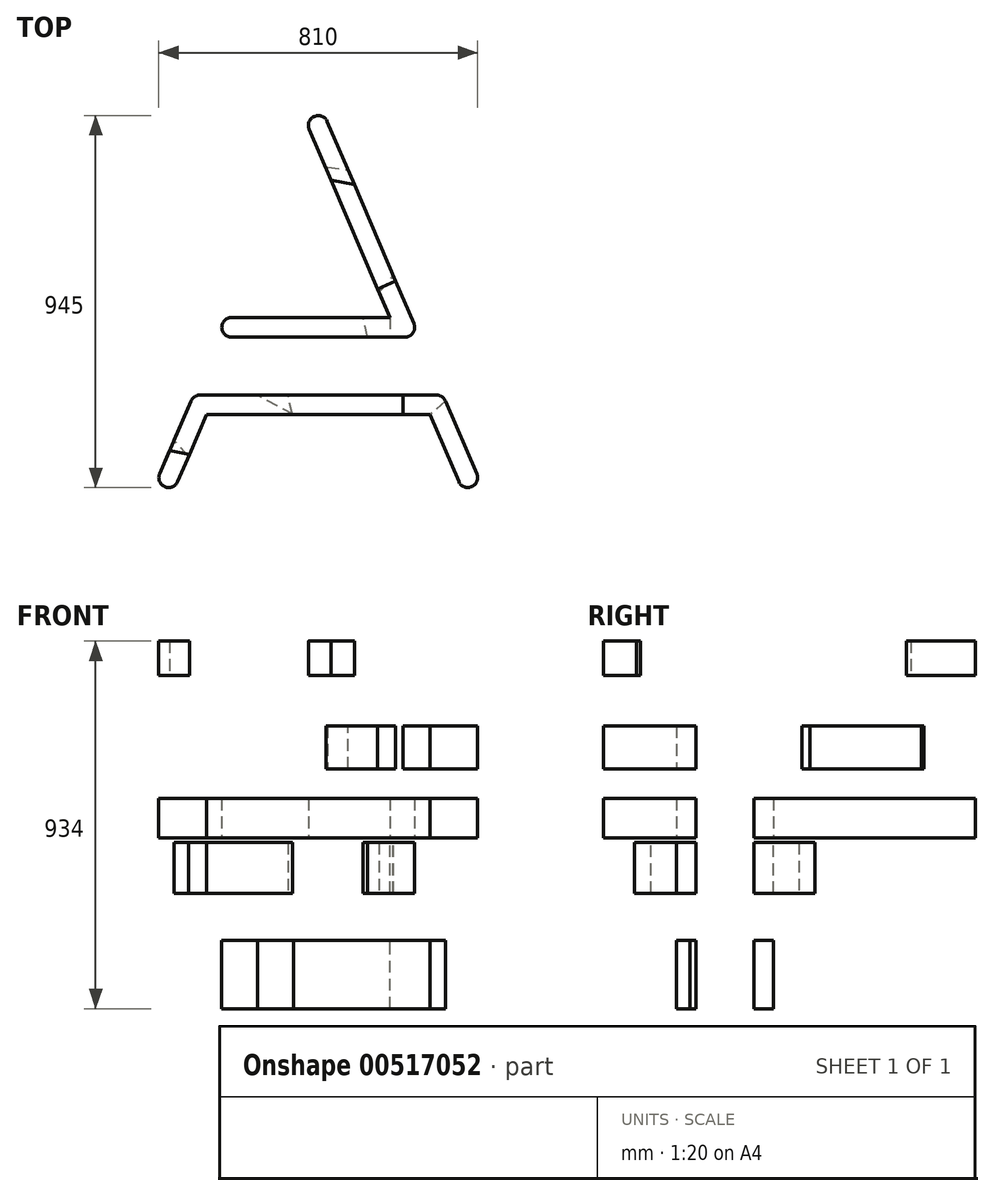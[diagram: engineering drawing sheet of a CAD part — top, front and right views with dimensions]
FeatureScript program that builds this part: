
annotation { "Feature Type Name" : "Feature", "Feature Type Description" : "" }
export const myFeature = defineFeature(function(context is Context, id is Id, definition is map)
    precondition{}
    {
        {
            var Q0;
            Q0=qCreatedBy(makeId("Top.planeOp"),FACE);
            var sketch = newSketch(context, id + "F0", { "sketchPlane" : qUnion([Q0])});
            skLineSegment(sketch, "E0", {"start": v(4.38, -239.2) * mm, "end": v(22.85, -239.2) * mm});
            skLineSegment(sketch, "E1", {"start": v(22.85, -239.2) * mm, "end": v(41.32, -239.2) * mm});
            skLineSegment(sketch, "E2", {"start": v(41.32, -239.2) * mm, "end": v(59.79, -239.2) * mm});
            skLineSegment(sketch, "E3", {"start": v(59.79, -239.2) * mm, "end": v(78.26, -239.2) * mm});
            skLineSegment(sketch, "E4", {"start": v(78.26, -239.2) * mm, "end": v(96.73, -239.2) * mm});
            skLineSegment(sketch, "E5", {"start": v(96.73, -239.2) * mm, "end": v(115.2, -239.2) * mm});
            skLineSegment(sketch, "E6", {"start": v(115.2, -239.2) * mm, "end": v(133.66, -239.2) * mm});
            skLineSegment(sketch, "E7", {"start": v(133.66, -239.2) * mm, "end": v(152.13, -239.2) * mm});
            skLineSegment(sketch, "E8", {"start": v(152.13, -239.2) * mm, "end": v(170.6, -239.2) * mm});
            skLineSegment(sketch, "E9", {"start": v(170.6, -239.2) * mm, "end": v(189.07, -239.2) * mm});
            skLineSegment(sketch, "E10", {"start": v(189.07, -239.2) * mm, "end": v(207.53, -239.2) * mm});
            skLineSegment(sketch, "E11", {"start": v(207.53, -239.2) * mm, "end": v(226, -239.2) * mm});
            skLineSegment(sketch, "E12", {"start": v(226, -239.2) * mm, "end": v(244.47, -239.2) * mm});
            skLineSegment(sketch, "E13", {"start": v(244.47, -239.2) * mm, "end": v(262.94, -239.2) * mm});
            skLineSegment(sketch, "E14", {"start": v(262.94, -239.2) * mm, "end": v(281.4, -239.2) * mm});
            skLineSegment(sketch, "E15", {"start": v(281.4, -239.2) * mm, "end": v(299.88, -239.2) * mm});
            skLineSegment(sketch, "E16", {"start": v(299.88, -239.2) * mm, "end": v(302.32, -239.25) * mm});
            skLineSegment(sketch, "E17", {"start": v(302.32, -239.25) * mm, "end": v(304.6, -239.4) * mm});
            skLineSegment(sketch, "E18", {"start": v(304.6, -239.4) * mm, "end": v(306.73, -239.65) * mm});
            skLineSegment(sketch, "E19", {"start": v(306.73, -239.65) * mm, "end": v(308.7, -240.02) * mm});
            skLineSegment(sketch, "E20", {"start": v(308.7, -240.02) * mm, "end": v(310.55, -240.51) * mm});
            skLineSegment(sketch, "E21", {"start": v(310.55, -240.51) * mm, "end": v(312.26, -241.13) * mm});
            skLineSegment(sketch, "E22", {"start": v(312.26, -241.13) * mm, "end": v(313.86, -241.89) * mm});
            skLineSegment(sketch, "E23", {"start": v(313.86, -241.89) * mm, "end": v(315.35, -242.78) * mm});
            skLineSegment(sketch, "E24", {"start": v(315.35, -242.78) * mm, "end": v(316.74, -243.83) * mm});
            skLineSegment(sketch, "E25", {"start": v(316.74, -243.83) * mm, "end": v(318.05, -245.03) * mm});
            skLineSegment(sketch, "E26", {"start": v(318.05, -245.03) * mm, "end": v(319.27, -246.39) * mm});
            skLineSegment(sketch, "E27", {"start": v(319.27, -246.39) * mm, "end": v(320.43, -247.92) * mm});
            skLineSegment(sketch, "E28", {"start": v(320.43, -247.92) * mm, "end": v(321.53, -249.63) * mm});
            skLineSegment(sketch, "E29", {"start": v(321.53, -249.63) * mm, "end": v(322.58, -251.52) * mm});
            skLineSegment(sketch, "E30", {"start": v(322.58, -251.52) * mm, "end": v(323.6, -253.6) * mm});
            skLineSegment(sketch, "E31", {"start": v(323.6, -253.6) * mm, "end": v(324.58, -255.88) * mm});
            skLineSegment(sketch, "E32", {"start": v(324.58, -255.88) * mm, "end": v(329.18, -267.18) * mm});
            skLineSegment(sketch, "E33", {"start": v(329.18, -267.18) * mm, "end": v(333.78, -278.48) * mm});
            skLineSegment(sketch, "E34", {"start": v(333.78, -278.48) * mm, "end": v(338.38, -289.78) * mm});
            skLineSegment(sketch, "E35", {"start": v(338.38, -289.78) * mm, "end": v(342.98, -301.08) * mm});
            skLineSegment(sketch, "E36", {"start": v(342.98, -301.08) * mm, "end": v(347.58, -312.38) * mm});
            skLineSegment(sketch, "E37", {"start": v(347.58, -312.38) * mm, "end": v(352.18, -323.68) * mm});
            skLineSegment(sketch, "E38", {"start": v(352.18, -323.68) * mm, "end": v(356.78, -334.98) * mm});
            skLineSegment(sketch, "E39", {"start": v(356.78, -334.98) * mm, "end": v(361.37, -346.29) * mm});
            skLineSegment(sketch, "E40", {"start": v(361.37, -346.29) * mm, "end": v(365.97, -357.59) * mm});
            skLineSegment(sketch, "E41", {"start": v(365.97, -357.59) * mm, "end": v(370.57, -368.89) * mm});
            skLineSegment(sketch, "E42", {"start": v(370.57, -368.89) * mm, "end": v(375.16, -380.19) * mm});
            skLineSegment(sketch, "E43", {"start": v(375.16, -380.19) * mm, "end": v(379.76, -391.5) * mm});
            skLineSegment(sketch, "E44", {"start": v(379.76, -391.5) * mm, "end": v(384.35, -402.8) * mm});
            skLineSegment(sketch, "E45", {"start": v(384.35, -402.8) * mm, "end": v(388.95, -414.1) * mm});
            skLineSegment(sketch, "E46", {"start": v(388.95, -414.1) * mm, "end": v(393.54, -425.4) * mm});
            skLineSegment(sketch, "E47", {"start": v(393.54, -425.4) * mm, "end": v(398.13, -436.7) * mm});
            skLineSegment(sketch, "E48", {"start": v(398.13, -436.7) * mm, "end": v(399, -439.11) * mm});
            skLineSegment(sketch, "E49", {"start": v(399, -439.11) * mm, "end": v(399.66, -441.5) * mm});
            skLineSegment(sketch, "E50", {"start": v(399.66, -441.5) * mm, "end": v(400.09, -443.83) * mm});
            skLineSegment(sketch, "E51", {"start": v(400.09, -443.83) * mm, "end": v(400.3, -446.11) * mm});
            skLineSegment(sketch, "E52", {"start": v(400.3, -446.11) * mm, "end": v(400.3, -448.34) * mm});
            skLineSegment(sketch, "E53", {"start": v(400.3, -448.34) * mm, "end": v(400.08, -450.5) * mm});
            skLineSegment(sketch, "E54", {"start": v(400.08, -450.5) * mm, "end": v(399.65, -452.58) * mm});
            skLineSegment(sketch, "E55", {"start": v(399.65, -452.58) * mm, "end": v(399.02, -454.58) * mm});
            skLineSegment(sketch, "E56", {"start": v(399.02, -454.58) * mm, "end": v(398.19, -456.5) * mm});
            skLineSegment(sketch, "E57", {"start": v(398.19, -456.5) * mm, "end": v(397.16, -458.3) * mm});
            skLineSegment(sketch, "E58", {"start": v(397.16, -458.3) * mm, "end": v(395.93, -460.01) * mm});
            skLineSegment(sketch, "E59", {"start": v(395.93, -460.01) * mm, "end": v(394.51, -461.6) * mm});
            skLineSegment(sketch, "E60", {"start": v(394.51, -461.6) * mm, "end": v(392.9, -463.08) * mm});
            skLineSegment(sketch, "E61", {"start": v(392.9, -463.08) * mm, "end": v(391.1, -464.41) * mm});
            skLineSegment(sketch, "E62", {"start": v(391.1, -464.41) * mm, "end": v(389.13, -465.61) * mm});
            skLineSegment(sketch, "E63", {"start": v(389.13, -465.61) * mm, "end": v(386.97, -466.67) * mm});
            skLineSegment(sketch, "E64", {"start": v(386.97, -466.67) * mm, "end": v(384.89, -467.45) * mm});
            skLineSegment(sketch, "E65", {"start": v(384.89, -467.45) * mm, "end": v(382.79, -468.02) * mm});
            skLineSegment(sketch, "E66", {"start": v(382.79, -468.02) * mm, "end": v(380.69, -468.35) * mm});
            skLineSegment(sketch, "E67", {"start": v(380.69, -468.35) * mm, "end": v(378.6, -468.47) * mm});
            skLineSegment(sketch, "E68", {"start": v(378.6, -468.47) * mm, "end": v(376.53, -468.36) * mm});
            skLineSegment(sketch, "E69", {"start": v(376.53, -468.36) * mm, "end": v(374.5, -468.05) * mm});
            skLineSegment(sketch, "E70", {"start": v(374.5, -468.05) * mm, "end": v(372.5, -467.52) * mm});
            skLineSegment(sketch, "E71", {"start": v(372.5, -467.52) * mm, "end": v(370.56, -466.79) * mm});
            skLineSegment(sketch, "E72", {"start": v(370.56, -466.79) * mm, "end": v(368.69, -465.85) * mm});
            skLineSegment(sketch, "E73", {"start": v(368.69, -465.85) * mm, "end": v(366.9, -464.71) * mm});
            skLineSegment(sketch, "E74", {"start": v(366.9, -464.71) * mm, "end": v(365.19, -463.38) * mm});
            skLineSegment(sketch, "E75", {"start": v(365.19, -463.38) * mm, "end": v(363.58, -461.85) * mm});
            skLineSegment(sketch, "E76", {"start": v(363.58, -461.85) * mm, "end": v(362.08, -460.13) * mm});
            skLineSegment(sketch, "E77", {"start": v(362.08, -460.13) * mm, "end": v(360.71, -458.23) * mm});
            skLineSegment(sketch, "E78", {"start": v(360.71, -458.23) * mm, "end": v(359.47, -456.14) * mm});
            skLineSegment(sketch, "E79", {"start": v(359.47, -456.14) * mm, "end": v(358.38, -453.87) * mm});
            skLineSegment(sketch, "E80", {"start": v(358.38, -453.87) * mm, "end": v(356.95, -450.55) * mm});
            skLineSegment(sketch, "E81", {"start": v(356.95, -450.55) * mm, "end": v(355.54, -447.22) * mm});
            skLineSegment(sketch, "E82", {"start": v(355.54, -447.22) * mm, "end": v(354.13, -443.88) * mm});
            skLineSegment(sketch, "E83", {"start": v(354.13, -443.88) * mm, "end": v(352.74, -440.54) * mm});
            skLineSegment(sketch, "E84", {"start": v(352.74, -440.54) * mm, "end": v(351.36, -437.2) * mm});
            skLineSegment(sketch, "E85", {"start": v(351.36, -437.2) * mm, "end": v(349.98, -433.85) * mm});
            skLineSegment(sketch, "E86", {"start": v(349.98, -433.85) * mm, "end": v(348.61, -430.5) * mm});
            skLineSegment(sketch, "E87", {"start": v(348.61, -430.5) * mm, "end": v(347.25, -427.14) * mm});
            skLineSegment(sketch, "E88", {"start": v(347.25, -427.14) * mm, "end": v(345.9, -423.79) * mm});
            skLineSegment(sketch, "E89", {"start": v(345.9, -423.79) * mm, "end": v(344.54, -420.43) * mm});
            skLineSegment(sketch, "E90", {"start": v(344.54, -420.43) * mm, "end": v(343.19, -417.07) * mm});
            skLineSegment(sketch, "E91", {"start": v(343.19, -417.07) * mm, "end": v(341.83, -413.71) * mm});
            skLineSegment(sketch, "E92", {"start": v(341.83, -413.71) * mm, "end": v(340.48, -410.36) * mm});
            skLineSegment(sketch, "E93", {"start": v(340.48, -410.36) * mm, "end": v(339.13, -407) * mm});
            skLineSegment(sketch, "E94", {"start": v(339.13, -407) * mm, "end": v(337.77, -403.64) * mm});
            skLineSegment(sketch, "E95", {"start": v(337.77, -403.64) * mm, "end": v(336.4, -400.29) * mm});
            skLineSegment(sketch, "E96", {"start": v(336.4, -400.29) * mm, "end": v(333.53, -393.2) * mm});
            skLineSegment(sketch, "E97", {"start": v(333.53, -393.2) * mm, "end": v(330.65, -386.13) * mm});
            skLineSegment(sketch, "E98", {"start": v(330.65, -386.13) * mm, "end": v(327.76, -379.05) * mm});
            skLineSegment(sketch, "E99", {"start": v(327.76, -379.05) * mm, "end": v(324.88, -371.96) * mm});
            skLineSegment(sketch, "E100", {"start": v(324.88, -371.96) * mm, "end": v(322, -364.88) * mm});
            skLineSegment(sketch, "E101", {"start": v(322, -364.88) * mm, "end": v(319.12, -357.8) * mm});
            skLineSegment(sketch, "E102", {"start": v(319.12, -357.8) * mm, "end": v(316.24, -350.72) * mm});
            skLineSegment(sketch, "E103", {"start": v(316.24, -350.72) * mm, "end": v(313.37, -343.63) * mm});
            skLineSegment(sketch, "E104", {"start": v(313.37, -343.63) * mm, "end": v(310.5, -336.55) * mm});
            skLineSegment(sketch, "E105", {"start": v(310.5, -336.55) * mm, "end": v(307.62, -329.47) * mm});
            skLineSegment(sketch, "E106", {"start": v(307.62, -329.47) * mm, "end": v(304.74, -322.38) * mm});
            skLineSegment(sketch, "E107", {"start": v(304.74, -322.38) * mm, "end": v(301.87, -315.3) * mm});
            skLineSegment(sketch, "E108", {"start": v(301.87, -315.3) * mm, "end": v(299, -308.2) * mm});
            skLineSegment(sketch, "E109", {"start": v(299, -308.2) * mm, "end": v(296.14, -301.12) * mm});
            skLineSegment(sketch, "E110", {"start": v(296.14, -301.12) * mm, "end": v(293.28, -294.03) * mm});
            skLineSegment(sketch, "E111", {"start": v(293.28, -294.03) * mm, "end": v(290.42, -286.94) * mm});
            skLineSegment(sketch, "E112", {"start": v(290.42, -286.94) * mm, "end": v(290.17, -286.36) * mm});
            skLineSegment(sketch, "E113", {"start": v(290.17, -286.36) * mm, "end": v(289.91, -285.82) * mm});
            skLineSegment(sketch, "E114", {"start": v(289.91, -285.82) * mm, "end": v(289.64, -285.32) * mm});
            skLineSegment(sketch, "E115", {"start": v(289.64, -285.32) * mm, "end": v(289.36, -284.87) * mm});
            skLineSegment(sketch, "E116", {"start": v(289.36, -284.87) * mm, "end": v(289.07, -284.46) * mm});
            skLineSegment(sketch, "E117", {"start": v(289.07, -284.46) * mm, "end": v(288.75, -284.1) * mm});
            skLineSegment(sketch, "E118", {"start": v(288.75, -284.1) * mm, "end": v(288.41, -283.77) * mm});
            skLineSegment(sketch, "E119", {"start": v(288.41, -283.77) * mm, "end": v(288.05, -283.48) * mm});
            skLineSegment(sketch, "E120", {"start": v(288.05, -283.48) * mm, "end": v(287.66, -283.23) * mm});
            skLineSegment(sketch, "E121", {"start": v(287.66, -283.23) * mm, "end": v(287.24, -283.02) * mm});
            skLineSegment(sketch, "E122", {"start": v(287.24, -283.02) * mm, "end": v(286.78, -282.84) * mm});
            skLineSegment(sketch, "E123", {"start": v(286.78, -282.84) * mm, "end": v(286.3, -282.7) * mm});
            skLineSegment(sketch, "E124", {"start": v(286.3, -282.7) * mm, "end": v(285.77, -282.6) * mm});
            skLineSegment(sketch, "E125", {"start": v(285.77, -282.6) * mm, "end": v(285.2, -282.51) * mm});
            skLineSegment(sketch, "E126", {"start": v(285.2, -282.51) * mm, "end": v(284.59, -282.47) * mm});
            skLineSegment(sketch, "E127", {"start": v(284.59, -282.47) * mm, "end": v(283.93, -282.46) * mm});
            skLineSegment(sketch, "E128", {"start": v(283.93, -282.46) * mm, "end": v(261.52, -282.47) * mm});
            skLineSegment(sketch, "E129", {"start": v(261.52, -282.47) * mm, "end": v(239.12, -282.48) * mm});
            skLineSegment(sketch, "E130", {"start": v(239.12, -282.48) * mm, "end": v(216.71, -282.48) * mm});
            skLineSegment(sketch, "E131", {"start": v(216.71, -282.48) * mm, "end": v(194.3, -282.49) * mm});
            skLineSegment(sketch, "E132", {"start": v(194.3, -282.49) * mm, "end": v(171.9, -282.49) * mm});
            skLineSegment(sketch, "E133", {"start": v(171.9, -282.49) * mm, "end": v(149.5, -282.49) * mm});
            skLineSegment(sketch, "E134", {"start": v(149.5, -282.49) * mm, "end": v(127.1, -282.49) * mm});
            skLineSegment(sketch, "E135", {"start": v(127.1, -282.49) * mm, "end": v(104.69, -282.48) * mm});
            skLineSegment(sketch, "E136", {"start": v(104.69, -282.48) * mm, "end": v(82.28, -282.48) * mm});
            skLineSegment(sketch, "E137", {"start": v(82.28, -282.48) * mm, "end": v(59.88, -282.47) * mm});
            skLineSegment(sketch, "E138", {"start": v(59.88, -282.47) * mm, "end": v(37.47, -282.47) * mm});
            skLineSegment(sketch, "E139", {"start": v(37.47, -282.47) * mm, "end": v(15.07, -282.46) * mm});
            skLineSegment(sketch, "E140", {"start": v(15.07, -282.46) * mm, "end": v(-7.34, -282.46) * mm});
            skLineSegment(sketch, "E141", {"start": v(-7.34, -282.46) * mm, "end": v(-29.74, -282.45) * mm});
            skLineSegment(sketch, "E142", {"start": v(-29.74, -282.45) * mm, "end": v(-52.15, -282.45) * mm});
            skLineSegment(sketch, "E143", {"start": v(-52.15, -282.45) * mm, "end": v(-74.56, -282.45) * mm});
            skLineSegment(sketch, "E144", {"start": v(-74.56, -282.45) * mm, "end": v(-87.15, -282.45) * mm});
            skLineSegment(sketch, "E145", {"start": v(-87.15, -282.45) * mm, "end": v(-99.74, -282.45) * mm});
            skLineSegment(sketch, "E146", {"start": v(-99.74, -282.45) * mm, "end": v(-112.33, -282.45) * mm});
            skLineSegment(sketch, "E147", {"start": v(-112.33, -282.45) * mm, "end": v(-124.93, -282.46) * mm});
            skLineSegment(sketch, "E148", {"start": v(-124.93, -282.46) * mm, "end": v(-137.52, -282.47) * mm});
            skLineSegment(sketch, "E149", {"start": v(-137.52, -282.47) * mm, "end": v(-150.11, -282.47) * mm});
            skLineSegment(sketch, "E150", {"start": v(-150.11, -282.47) * mm, "end": v(-162.7, -282.48) * mm});
            skLineSegment(sketch, "E151", {"start": v(-162.7, -282.48) * mm, "end": v(-175.3, -282.48) * mm});
            skLineSegment(sketch, "E152", {"start": v(-175.3, -282.48) * mm, "end": v(-187.9, -282.49) * mm});
            skLineSegment(sketch, "E153", {"start": v(-187.9, -282.49) * mm, "end": v(-200.49, -282.49) * mm});
            skLineSegment(sketch, "E154", {"start": v(-200.49, -282.49) * mm, "end": v(-213.08, -282.5) * mm});
            skLineSegment(sketch, "E155", {"start": v(-213.08, -282.5) * mm, "end": v(-225.67, -282.49) * mm});
            skLineSegment(sketch, "E156", {"start": v(-225.67, -282.49) * mm, "end": v(-238.26, -282.48) * mm});
            skLineSegment(sketch, "E157", {"start": v(-238.26, -282.48) * mm, "end": v(-250.86, -282.47) * mm});
            skLineSegment(sketch, "E158", {"start": v(-250.86, -282.47) * mm, "end": v(-263.45, -282.46) * mm});
            skLineSegment(sketch, "E159", {"start": v(-263.45, -282.46) * mm, "end": v(-276.04, -282.44) * mm});
            skLineSegment(sketch, "E160", {"start": v(-276.04, -282.44) * mm, "end": v(-276.75, -282.46) * mm});
            skLineSegment(sketch, "E161", {"start": v(-276.75, -282.46) * mm, "end": v(-277.42, -282.5) * mm});
            skLineSegment(sketch, "E162", {"start": v(-277.42, -282.5) * mm, "end": v(-278.05, -282.57) * mm});
            skLineSegment(sketch, "E163", {"start": v(-278.05, -282.57) * mm, "end": v(-278.63, -282.68) * mm});
            skLineSegment(sketch, "E164", {"start": v(-278.63, -282.68) * mm, "end": v(-279.18, -282.81) * mm});
            skLineSegment(sketch, "E165", {"start": v(-279.18, -282.81) * mm, "end": v(-279.7, -283) * mm});
            skLineSegment(sketch, "E166", {"start": v(-279.7, -283) * mm, "end": v(-280.17, -283.2) * mm});
            skLineSegment(sketch, "E167", {"start": v(-280.17, -283.2) * mm, "end": v(-280.62, -283.46) * mm});
            skLineSegment(sketch, "E168", {"start": v(-280.62, -283.46) * mm, "end": v(-281.05, -283.75) * mm});
            skLineSegment(sketch, "E169", {"start": v(-281.05, -283.75) * mm, "end": v(-281.45, -284.1) * mm});
            skLineSegment(sketch, "E170", {"start": v(-281.45, -284.1) * mm, "end": v(-281.83, -284.48) * mm});
            skLineSegment(sketch, "E171", {"start": v(-281.83, -284.48) * mm, "end": v(-282.18, -284.91) * mm});
            skLineSegment(sketch, "E172", {"start": v(-282.18, -284.91) * mm, "end": v(-282.53, -285.4) * mm});
            skLineSegment(sketch, "E173", {"start": v(-282.53, -285.4) * mm, "end": v(-282.85, -285.93) * mm});
            skLineSegment(sketch, "E174", {"start": v(-282.85, -285.93) * mm, "end": v(-283.17, -286.52) * mm});
            skLineSegment(sketch, "E175", {"start": v(-283.17, -286.52) * mm, "end": v(-283.48, -287.16) * mm});
            skLineSegment(sketch, "E176", {"start": v(-283.48, -287.16) * mm, "end": v(-288.23, -297.71) * mm});
            skLineSegment(sketch, "E177", {"start": v(-288.23, -297.71) * mm, "end": v(-293, -308.27) * mm});
            skLineSegment(sketch, "E178", {"start": v(-293, -308.27) * mm, "end": v(-297.76, -318.82) * mm});
            skLineSegment(sketch, "E179", {"start": v(-297.76, -318.82) * mm, "end": v(-302.52, -329.37) * mm});
            skLineSegment(sketch, "E180", {"start": v(-302.52, -329.37) * mm, "end": v(-307.3, -339.92) * mm});
            skLineSegment(sketch, "E181", {"start": v(-307.3, -339.92) * mm, "end": v(-312.06, -350.46) * mm});
            skLineSegment(sketch, "E182", {"start": v(-312.06, -350.46) * mm, "end": v(-316.84, -361.01) * mm});
            skLineSegment(sketch, "E183", {"start": v(-316.84, -361.01) * mm, "end": v(-321.61, -371.56) * mm});
            skLineSegment(sketch, "E184", {"start": v(-321.61, -371.56) * mm, "end": v(-326.39, -382.1) * mm});
            skLineSegment(sketch, "E185", {"start": v(-326.39, -382.1) * mm, "end": v(-331.17, -392.65) * mm});
            skLineSegment(sketch, "E186", {"start": v(-331.17, -392.65) * mm, "end": v(-335.95, -403.2) * mm});
            skLineSegment(sketch, "E187", {"start": v(-335.95, -403.2) * mm, "end": v(-340.73, -413.74) * mm});
            skLineSegment(sketch, "E188", {"start": v(-340.73, -413.74) * mm, "end": v(-345.5, -424.28) * mm});
            skLineSegment(sketch, "E189", {"start": v(-345.5, -424.28) * mm, "end": v(-350.29, -434.82) * mm});
            skLineSegment(sketch, "E190", {"start": v(-350.29, -434.82) * mm, "end": v(-355.07, -445.37) * mm});
            skLineSegment(sketch, "E191", {"start": v(-355.07, -445.37) * mm, "end": v(-359.85, -455.9) * mm});
            skLineSegment(sketch, "E192", {"start": v(-359.85, -455.9) * mm, "end": v(-360.64, -457.5) * mm});
            skLineSegment(sketch, "E193", {"start": v(-360.64, -457.5) * mm, "end": v(-361.53, -458.99) * mm});
            skLineSegment(sketch, "E194", {"start": v(-361.53, -458.99) * mm, "end": v(-362.51, -460.37) * mm});
            skLineSegment(sketch, "E195", {"start": v(-362.51, -460.37) * mm, "end": v(-363.58, -461.65) * mm});
            skLineSegment(sketch, "E196", {"start": v(-363.58, -461.65) * mm, "end": v(-364.73, -462.83) * mm});
            skLineSegment(sketch, "E197", {"start": v(-364.73, -462.83) * mm, "end": v(-365.96, -463.9) * mm});
            skLineSegment(sketch, "E198", {"start": v(-365.96, -463.9) * mm, "end": v(-367.26, -464.85) * mm});
            skLineSegment(sketch, "E199", {"start": v(-367.26, -464.85) * mm, "end": v(-368.64, -465.7) * mm});
            skLineSegment(sketch, "E200", {"start": v(-368.64, -465.7) * mm, "end": v(-370.09, -466.42) * mm});
            skLineSegment(sketch, "E201", {"start": v(-370.09, -466.42) * mm, "end": v(-371.6, -467.03) * mm});
            skLineSegment(sketch, "E202", {"start": v(-371.6, -467.03) * mm, "end": v(-373.17, -467.53) * mm});
            skLineSegment(sketch, "E203", {"start": v(-373.17, -467.53) * mm, "end": v(-374.8, -467.9) * mm});
            skLineSegment(sketch, "E204", {"start": v(-374.8, -467.9) * mm, "end": v(-376.47, -468.15) * mm});
            skLineSegment(sketch, "E205", {"start": v(-376.47, -468.15) * mm, "end": v(-378.2, -468.28) * mm});
            skLineSegment(sketch, "E206", {"start": v(-378.2, -468.28) * mm, "end": v(-379.96, -468.29) * mm});
            skLineSegment(sketch, "E207", {"start": v(-379.96, -468.29) * mm, "end": v(-381.77, -468.16) * mm});
            skLineSegment(sketch, "E208", {"start": v(-381.77, -468.16) * mm, "end": v(-383.48, -467.92) * mm});
            skLineSegment(sketch, "E209", {"start": v(-383.48, -467.92) * mm, "end": v(-385.15, -467.57) * mm});
            skLineSegment(sketch, "E210", {"start": v(-385.15, -467.57) * mm, "end": v(-386.78, -467.1) * mm});
            skLineSegment(sketch, "E211", {"start": v(-386.78, -467.1) * mm, "end": v(-388.34, -466.53) * mm});
            skLineSegment(sketch, "E212", {"start": v(-388.34, -466.53) * mm, "end": v(-389.84, -465.85) * mm});
            skLineSegment(sketch, "E213", {"start": v(-389.84, -465.85) * mm, "end": v(-391.27, -465.07) * mm});
            skLineSegment(sketch, "E214", {"start": v(-391.27, -465.07) * mm, "end": v(-392.63, -464.19) * mm});
            skLineSegment(sketch, "E215", {"start": v(-392.63, -464.19) * mm, "end": v(-393.89, -463.21) * mm});
            skLineSegment(sketch, "E216", {"start": v(-393.89, -463.21) * mm, "end": v(-395.06, -462.14) * mm});
            skLineSegment(sketch, "E217", {"start": v(-395.06, -462.14) * mm, "end": v(-396.13, -460.98) * mm});
            skLineSegment(sketch, "E218", {"start": v(-396.13, -460.98) * mm, "end": v(-397.08, -459.74) * mm});
            skLineSegment(sketch, "E219", {"start": v(-397.08, -459.74) * mm, "end": v(-397.92, -458.4) * mm});
            skLineSegment(sketch, "E220", {"start": v(-397.92, -458.4) * mm, "end": v(-398.64, -457) * mm});
            skLineSegment(sketch, "E221", {"start": v(-398.64, -457) * mm, "end": v(-399.22, -455.51) * mm});
            skLineSegment(sketch, "E222", {"start": v(-399.22, -455.51) * mm, "end": v(-399.66, -453.95) * mm});
            skLineSegment(sketch, "E223", {"start": v(-399.66, -453.95) * mm, "end": v(-399.96, -452.32) * mm});
            skLineSegment(sketch, "E224", {"start": v(-399.96, -452.32) * mm, "end": v(-400.08, -451.27) * mm});
            skLineSegment(sketch, "E225", {"start": v(-400.08, -451.27) * mm, "end": v(-400.18, -450.2) * mm});
            skLineSegment(sketch, "E226", {"start": v(-400.18, -450.2) * mm, "end": v(-400.25, -449.13) * mm});
            skLineSegment(sketch, "E227", {"start": v(-400.25, -449.13) * mm, "end": v(-400.29, -448.04) * mm});
            skLineSegment(sketch, "E228", {"start": v(-400.29, -448.04) * mm, "end": v(-400.3, -446.94) * mm});
            skLineSegment(sketch, "E229", {"start": v(-400.3, -446.94) * mm, "end": v(-400.28, -445.84) * mm});
            skLineSegment(sketch, "E230", {"start": v(-400.28, -445.84) * mm, "end": v(-400.22, -444.73) * mm});
            skLineSegment(sketch, "E231", {"start": v(-400.22, -444.73) * mm, "end": v(-400.14, -443.63) * mm});
            skLineSegment(sketch, "E232", {"start": v(-400.14, -443.63) * mm, "end": v(-400.02, -442.53) * mm});
            skLineSegment(sketch, "E233", {"start": v(-400.02, -442.53) * mm, "end": v(-399.86, -441.45) * mm});
            skLineSegment(sketch, "E234", {"start": v(-399.86, -441.45) * mm, "end": v(-399.67, -440.38) * mm});
            skLineSegment(sketch, "E235", {"start": v(-399.67, -440.38) * mm, "end": v(-399.43, -439.32) * mm});
            skLineSegment(sketch, "E236", {"start": v(-399.43, -439.32) * mm, "end": v(-399.16, -438.29) * mm});
            skLineSegment(sketch, "E237", {"start": v(-399.16, -438.29) * mm, "end": v(-398.85, -437.28) * mm});
            skLineSegment(sketch, "E238", {"start": v(-398.85, -437.28) * mm, "end": v(-398.5, -436.3) * mm});
            skLineSegment(sketch, "E239", {"start": v(-398.5, -436.3) * mm, "end": v(-398.1, -435.34) * mm});
            skLineSegment(sketch, "E240", {"start": v(-398.1, -435.34) * mm, "end": v(-392.92, -423.78) * mm});
            skLineSegment(sketch, "E241", {"start": v(-392.92, -423.78) * mm, "end": v(-387.74, -412.22) * mm});
            skLineSegment(sketch, "E242", {"start": v(-387.74, -412.22) * mm, "end": v(-382.54, -400.66) * mm});
            skLineSegment(sketch, "E243", {"start": v(-382.54, -400.66) * mm, "end": v(-377.34, -389.1) * mm});
            skLineSegment(sketch, "E244", {"start": v(-377.34, -389.1) * mm, "end": v(-372.13, -377.56) * mm});
            skLineSegment(sketch, "E245", {"start": v(-372.13, -377.56) * mm, "end": v(-366.91, -366.01) * mm});
            skLineSegment(sketch, "E246", {"start": v(-366.91, -366.01) * mm, "end": v(-361.69, -354.47) * mm});
            skLineSegment(sketch, "E247", {"start": v(-361.69, -354.47) * mm, "end": v(-356.46, -342.93) * mm});
            skLineSegment(sketch, "E248", {"start": v(-356.46, -342.93) * mm, "end": v(-351.23, -331.39) * mm});
            skLineSegment(sketch, "E249", {"start": v(-351.23, -331.39) * mm, "end": v(-346, -319.85) * mm});
            skLineSegment(sketch, "E250", {"start": v(-346, -319.85) * mm, "end": v(-340.76, -308.31) * mm});
            skLineSegment(sketch, "E251", {"start": v(-340.76, -308.31) * mm, "end": v(-335.52, -296.77) * mm});
            skLineSegment(sketch, "E252", {"start": v(-335.52, -296.77) * mm, "end": v(-330.28, -285.24) * mm});
            skLineSegment(sketch, "E253", {"start": v(-330.28, -285.24) * mm, "end": v(-325.04, -273.7) * mm});
            skLineSegment(sketch, "E254", {"start": v(-325.04, -273.7) * mm, "end": v(-319.8, -262.17) * mm});
            skLineSegment(sketch, "E255", {"start": v(-319.8, -262.17) * mm, "end": v(-314.56, -250.63) * mm});
            skLineSegment(sketch, "E256", {"start": v(-314.56, -250.63) * mm, "end": v(-313.9, -249.32) * mm});
            skLineSegment(sketch, "E257", {"start": v(-313.9, -249.32) * mm, "end": v(-313.2, -248.1) * mm});
            skLineSegment(sketch, "E258", {"start": v(-313.2, -248.1) * mm, "end": v(-312.43, -246.97) * mm});
            skLineSegment(sketch, "E259", {"start": v(-312.43, -246.97) * mm, "end": v(-311.6, -245.91) * mm});
            skLineSegment(sketch, "E260", {"start": v(-311.6, -245.91) * mm, "end": v(-310.72, -244.94) * mm});
            skLineSegment(sketch, "E261", {"start": v(-310.72, -244.94) * mm, "end": v(-309.78, -244.05) * mm});
            skLineSegment(sketch, "E262", {"start": v(-309.78, -244.05) * mm, "end": v(-308.79, -243.24) * mm});
            skLineSegment(sketch, "E263", {"start": v(-308.79, -243.24) * mm, "end": v(-307.74, -242.51) * mm});
            skLineSegment(sketch, "E264", {"start": v(-307.74, -242.51) * mm, "end": v(-306.64, -241.86) * mm});
            skLineSegment(sketch, "E265", {"start": v(-306.64, -241.86) * mm, "end": v(-305.49, -241.28) * mm});
            skLineSegment(sketch, "E266", {"start": v(-305.49, -241.28) * mm, "end": v(-304.29, -240.77) * mm});
            skLineSegment(sketch, "E267", {"start": v(-304.29, -240.77) * mm, "end": v(-303.04, -240.34) * mm});
            skLineSegment(sketch, "E268", {"start": v(-303.04, -240.34) * mm, "end": v(-301.74, -239.97) * mm});
            skLineSegment(sketch, "E269", {"start": v(-301.74, -239.97) * mm, "end": v(-300.4, -239.68) * mm});
            skLineSegment(sketch, "E270", {"start": v(-300.4, -239.68) * mm, "end": v(-299.03, -239.45) * mm});
            skLineSegment(sketch, "E271", {"start": v(-299.03, -239.45) * mm, "end": v(-297.6, -239.3) * mm});
            skLineSegment(sketch, "E272", {"start": v(-297.6, -239.3) * mm, "end": v(-297.2, -239.26) * mm});
            skLineSegment(sketch, "E273", {"start": v(-297.2, -239.26) * mm, "end": v(-296.8, -239.24) * mm});
            skLineSegment(sketch, "E274", {"start": v(-296.8, -239.24) * mm, "end": v(-296.4, -239.21) * mm});
            skLineSegment(sketch, "E275", {"start": v(-296.4, -239.21) * mm, "end": v(-295.99, -239.2) * mm});
            skLineSegment(sketch, "E276", {"start": v(-295.99, -239.2) * mm, "end": v(-295.58, -239.19) * mm});
            skLineSegment(sketch, "E277", {"start": v(-295.58, -239.19) * mm, "end": v(-295.17, -239.18) * mm});
            skLineSegment(sketch, "E278", {"start": v(-295.17, -239.18) * mm, "end": v(-294.77, -239.18) * mm});
            skLineSegment(sketch, "E279", {"start": v(-294.77, -239.18) * mm, "end": v(-294.36, -239.18) * mm});
            skLineSegment(sketch, "E280", {"start": v(-294.36, -239.18) * mm, "end": v(-293.95, -239.18) * mm});
            skLineSegment(sketch, "E281", {"start": v(-293.95, -239.18) * mm, "end": v(-293.55, -239.18) * mm});
            skLineSegment(sketch, "E282", {"start": v(-293.55, -239.18) * mm, "end": v(-293.14, -239.19) * mm});
            skLineSegment(sketch, "E283", {"start": v(-293.14, -239.19) * mm, "end": v(-292.73, -239.2) * mm});
            skLineSegment(sketch, "E284", {"start": v(-292.73, -239.2) * mm, "end": v(-292.33, -239.2) * mm});
            skLineSegment(sketch, "E285", {"start": v(-292.33, -239.2) * mm, "end": v(-291.92, -239.2) * mm});
            skLineSegment(sketch, "E286", {"start": v(-291.92, -239.2) * mm, "end": v(-291.51, -239.2) * mm});
            skLineSegment(sketch, "E287", {"start": v(-291.51, -239.2) * mm, "end": v(-291.1, -239.2) * mm});
            skLineSegment(sketch, "E288", {"start": v(-291.1, -239.2) * mm, "end": v(-272.64, -239.2) * mm});
            skLineSegment(sketch, "E289", {"start": v(-272.64, -239.2) * mm, "end": v(-254.17, -239.2) * mm});
            skLineSegment(sketch, "E290", {"start": v(-254.17, -239.2) * mm, "end": v(-235.7, -239.2) * mm});
            skLineSegment(sketch, "E291", {"start": v(-235.7, -239.2) * mm, "end": v(-217.23, -239.2) * mm});
            skLineSegment(sketch, "E292", {"start": v(-217.23, -239.2) * mm, "end": v(-198.77, -239.2) * mm});
            skLineSegment(sketch, "E293", {"start": v(-198.77, -239.2) * mm, "end": v(-180.3, -239.2) * mm});
            skLineSegment(sketch, "E294", {"start": v(-180.3, -239.2) * mm, "end": v(-161.83, -239.2) * mm});
            skLineSegment(sketch, "E295", {"start": v(-161.83, -239.2) * mm, "end": v(-143.36, -239.2) * mm});
            skLineSegment(sketch, "E296", {"start": v(-143.36, -239.2) * mm, "end": v(-124.9, -239.2) * mm});
            skLineSegment(sketch, "E297", {"start": v(-124.9, -239.2) * mm, "end": v(-106.43, -239.2) * mm});
            skLineSegment(sketch, "E298", {"start": v(-106.43, -239.2) * mm, "end": v(-87.96, -239.2) * mm});
            skLineSegment(sketch, "E299", {"start": v(-87.96, -239.2) * mm, "end": v(-69.49, -239.2) * mm});
            skLineSegment(sketch, "E300", {"start": v(-69.49, -239.2) * mm, "end": v(-51.02, -239.2) * mm});
            skLineSegment(sketch, "E301", {"start": v(-51.02, -239.2) * mm, "end": v(-32.55, -239.2) * mm});
            skLineSegment(sketch, "E302", {"start": v(-32.55, -239.2) * mm, "end": v(-14.08, -239.2) * mm});
            skLineSegment(sketch, "E303", {"start": v(-14.08, -239.2) * mm, "end": v(4.38, -239.2) * mm});
            skLineSegment(sketch, "E304", {"start": v(190.22, -42.46) * mm, "end": v(190.07, -42.05) * mm});
            skLineSegment(sketch, "E305", {"start": v(190.07, -42.05) * mm, "end": v(189.92, -41.65) * mm});
            skLineSegment(sketch, "E306", {"start": v(189.92, -41.65) * mm, "end": v(189.78, -41.26) * mm});
            skLineSegment(sketch, "E307", {"start": v(189.78, -41.26) * mm, "end": v(189.64, -40.88) * mm});
            skLineSegment(sketch, "E308", {"start": v(189.64, -40.88) * mm, "end": v(189.5, -40.51) * mm});
            skLineSegment(sketch, "E309", {"start": v(189.5, -40.51) * mm, "end": v(189.38, -40.15) * mm});
            skLineSegment(sketch, "E310", {"start": v(189.38, -40.15) * mm, "end": v(189.25, -39.8) * mm});
            skLineSegment(sketch, "E311", {"start": v(189.25, -39.8) * mm, "end": v(189.12, -39.46) * mm});
            skLineSegment(sketch, "E312", {"start": v(189.12, -39.46) * mm, "end": v(189, -39.12) * mm});
            skLineSegment(sketch, "E313", {"start": v(189, -39.12) * mm, "end": v(188.87, -38.79) * mm});
            skLineSegment(sketch, "E314", {"start": v(188.87, -38.79) * mm, "end": v(188.75, -38.46) * mm});
            skLineSegment(sketch, "E315", {"start": v(188.75, -38.46) * mm, "end": v(188.63, -38.14) * mm});
            skLineSegment(sketch, "E316", {"start": v(188.63, -38.14) * mm, "end": v(188.5, -37.82) * mm});
            skLineSegment(sketch, "E317", {"start": v(188.5, -37.82) * mm, "end": v(188.39, -37.5) * mm});
            skLineSegment(sketch, "E318", {"start": v(188.39, -37.5) * mm, "end": v(188.26, -37.2) * mm});
            skLineSegment(sketch, "E319", {"start": v(188.26, -37.2) * mm, "end": v(188.14, -36.88) * mm});
            skLineSegment(sketch, "E320", {"start": v(188.14, -36.88) * mm, "end": v(179.93, -16.85) * mm});
            skLineSegment(sketch, "E321", {"start": v(179.93, -16.85) * mm, "end": v(171.72, 3.2) * mm});
            skLineSegment(sketch, "E322", {"start": v(171.72, 3.2) * mm, "end": v(163.5, 23.23) * mm});
            skLineSegment(sketch, "E323", {"start": v(163.5, 23.23) * mm, "end": v(155.3, 43.27) * mm});
            skLineSegment(sketch, "E324", {"start": v(155.3, 43.27) * mm, "end": v(147.09, 63.3) * mm});
            skLineSegment(sketch, "E325", {"start": v(147.09, 63.3) * mm, "end": v(138.88, 83.34) * mm});
            skLineSegment(sketch, "E326", {"start": v(138.88, 83.34) * mm, "end": v(130.67, 103.38) * mm});
            skLineSegment(sketch, "E327", {"start": v(130.67, 103.38) * mm, "end": v(122.46, 123.42) * mm});
            skLineSegment(sketch, "E328", {"start": v(122.46, 123.42) * mm, "end": v(114.25, 143.45) * mm});
            skLineSegment(sketch, "E329", {"start": v(114.25, 143.45) * mm, "end": v(106.04, 163.5) * mm});
            skLineSegment(sketch, "E330", {"start": v(106.04, 163.5) * mm, "end": v(97.83, 183.53) * mm});
            skLineSegment(sketch, "E331", {"start": v(97.83, 183.53) * mm, "end": v(89.62, 203.57) * mm});
            skLineSegment(sketch, "E332", {"start": v(89.62, 203.57) * mm, "end": v(81.4, 223.6) * mm});
            skLineSegment(sketch, "E333", {"start": v(81.4, 223.6) * mm, "end": v(73.2, 243.64) * mm});
            skLineSegment(sketch, "E334", {"start": v(73.2, 243.64) * mm, "end": v(64.99, 263.68) * mm});
            skLineSegment(sketch, "E335", {"start": v(64.99, 263.68) * mm, "end": v(56.78, 283.72) * mm});
            skLineSegment(sketch, "E336", {"start": v(56.78, 283.72) * mm, "end": v(52.9, 293.19) * mm});
            skLineSegment(sketch, "E337", {"start": v(52.9, 293.19) * mm, "end": v(49.02, 302.66) * mm});
            skLineSegment(sketch, "E338", {"start": v(49.02, 302.66) * mm, "end": v(45.15, 312.13) * mm});
            skLineSegment(sketch, "E339", {"start": v(45.15, 312.13) * mm, "end": v(41.28, 321.6) * mm});
            skLineSegment(sketch, "E340", {"start": v(41.28, 321.6) * mm, "end": v(37.41, 331.07) * mm});
            skLineSegment(sketch, "E341", {"start": v(37.41, 331.07) * mm, "end": v(33.54, 340.55) * mm});
            skLineSegment(sketch, "E342", {"start": v(33.54, 340.55) * mm, "end": v(29.67, 350.02) * mm});
            skLineSegment(sketch, "E343", {"start": v(29.67, 350.02) * mm, "end": v(25.8, 359.5) * mm});
            skLineSegment(sketch, "E344", {"start": v(25.8, 359.5) * mm, "end": v(21.92, 368.96) * mm});
            skLineSegment(sketch, "E345", {"start": v(21.92, 368.96) * mm, "end": v(18.04, 378.43) * mm});
            skLineSegment(sketch, "E346", {"start": v(18.04, 378.43) * mm, "end": v(14.15, 387.9) * mm});
            skLineSegment(sketch, "E347", {"start": v(14.15, 387.9) * mm, "end": v(10.26, 397.36) * mm});
            skLineSegment(sketch, "E348", {"start": v(10.26, 397.36) * mm, "end": v(6.35, 406.81) * mm});
            skLineSegment(sketch, "E349", {"start": v(6.35, 406.81) * mm, "end": v(2.44, 416.27) * mm});
            skLineSegment(sketch, "E350", {"start": v(2.44, 416.27) * mm, "end": v(-1.48, 425.72) * mm});
            skLineSegment(sketch, "E351", {"start": v(-1.48, 425.72) * mm, "end": v(-5.41, 435.17) * mm});
            skLineSegment(sketch, "E352", {"start": v(-5.41, 435.17) * mm, "end": v(-6.4, 437.74) * mm});
            skLineSegment(sketch, "E353", {"start": v(-6.4, 437.74) * mm, "end": v(-7.16, 440.17) * mm});
            skLineSegment(sketch, "E354", {"start": v(-7.16, 440.17) * mm, "end": v(-7.7, 442.45) * mm});
            skLineSegment(sketch, "E355", {"start": v(-7.7, 442.45) * mm, "end": v(-8.06, 444.6) * mm});
            skLineSegment(sketch, "E356", {"start": v(-8.06, 444.6) * mm, "end": v(-8.22, 446.62) * mm});
            skLineSegment(sketch, "E357", {"start": v(-8.22, 446.62) * mm, "end": v(-8.2, 448.52) * mm});
            skLineSegment(sketch, "E358", {"start": v(-8.2, 448.52) * mm, "end": v(-8.02, 450.3) * mm});
            skLineSegment(sketch, "E359", {"start": v(-8.02, 450.3) * mm, "end": v(-7.68, 451.98) * mm});
            skLineSegment(sketch, "E360", {"start": v(-7.68, 451.98) * mm, "end": v(-7.21, 453.56) * mm});
            skLineSegment(sketch, "E361", {"start": v(-7.21, 453.56) * mm, "end": v(-6.62, 455.05) * mm});
            skLineSegment(sketch, "E362", {"start": v(-6.62, 455.05) * mm, "end": v(-5.9, 456.46) * mm});
            skLineSegment(sketch, "E363", {"start": v(-5.9, 456.46) * mm, "end": v(-5.1, 457.78) * mm});
            skLineSegment(sketch, "E364", {"start": v(-5.1, 457.78) * mm, "end": v(-4.2, 459.03) * mm});
            skLineSegment(sketch, "E365", {"start": v(-4.2, 459.03) * mm, "end": v(-3.22, 460.22) * mm});
            skLineSegment(sketch, "E366", {"start": v(-3.22, 460.22) * mm, "end": v(-2.18, 461.36) * mm});
            skLineSegment(sketch, "E367", {"start": v(-2.18, 461.36) * mm, "end": v(-1.1, 462.44) * mm});
            skLineSegment(sketch, "E368", {"start": v(-1.1, 462.44) * mm, "end": v(0.6, 463.9) * mm});
            skLineSegment(sketch, "E369", {"start": v(0.6, 463.9) * mm, "end": v(2.37, 465.17) * mm});
            skLineSegment(sketch, "E370", {"start": v(2.37, 465.17) * mm, "end": v(4.22, 466.23) * mm});
            skLineSegment(sketch, "E371", {"start": v(4.22, 466.23) * mm, "end": v(6.13, 467.09) * mm});
            skLineSegment(sketch, "E372", {"start": v(6.13, 467.09) * mm, "end": v(8.09, 467.74) * mm});
            skLineSegment(sketch, "E373", {"start": v(8.09, 467.74) * mm, "end": v(10.08, 468.18) * mm});
            skLineSegment(sketch, "E374", {"start": v(10.08, 468.18) * mm, "end": v(12.08, 468.43) * mm});
            skLineSegment(sketch, "E375", {"start": v(12.08, 468.43) * mm, "end": v(14.1, 468.47) * mm});
            skLineSegment(sketch, "E376", {"start": v(14.1, 468.47) * mm, "end": v(16.1, 468.3) * mm});
            skLineSegment(sketch, "E377", {"start": v(16.1, 468.3) * mm, "end": v(18.08, 467.93) * mm});
            skLineSegment(sketch, "E378", {"start": v(18.08, 467.93) * mm, "end": v(20.02, 467.36) * mm});
            skLineSegment(sketch, "E379", {"start": v(20.02, 467.36) * mm, "end": v(21.92, 466.58) * mm});
            skLineSegment(sketch, "E380", {"start": v(21.92, 466.58) * mm, "end": v(23.76, 465.6) * mm});
            skLineSegment(sketch, "E381", {"start": v(23.76, 465.6) * mm, "end": v(25.51, 464.41) * mm});
            skLineSegment(sketch, "E382", {"start": v(25.51, 464.41) * mm, "end": v(27.18, 463.02) * mm});
            skLineSegment(sketch, "E383", {"start": v(27.18, 463.02) * mm, "end": v(28.75, 461.43) * mm});
            skLineSegment(sketch, "E384", {"start": v(28.75, 461.43) * mm, "end": v(29.28, 460.8) * mm});
            skLineSegment(sketch, "E385", {"start": v(29.28, 460.8) * mm, "end": v(29.8, 460.16) * mm});
            skLineSegment(sketch, "E386", {"start": v(29.8, 460.16) * mm, "end": v(30.31, 459.5) * mm});
            skLineSegment(sketch, "E387", {"start": v(30.31, 459.5) * mm, "end": v(30.8, 458.83) * mm});
            skLineSegment(sketch, "E388", {"start": v(30.8, 458.83) * mm, "end": v(31.28, 458.14) * mm});
            skLineSegment(sketch, "E389", {"start": v(31.28, 458.14) * mm, "end": v(31.74, 457.43) * mm});
            skLineSegment(sketch, "E390", {"start": v(31.74, 457.43) * mm, "end": v(32.18, 456.72) * mm});
            skLineSegment(sketch, "E391", {"start": v(32.18, 456.72) * mm, "end": v(32.61, 456) * mm});
            skLineSegment(sketch, "E392", {"start": v(32.61, 456) * mm, "end": v(33.03, 455.25) * mm});
            skLineSegment(sketch, "E393", {"start": v(33.03, 455.25) * mm, "end": v(33.43, 454.5) * mm});
            skLineSegment(sketch, "E394", {"start": v(33.43, 454.5) * mm, "end": v(33.82, 453.76) * mm});
            skLineSegment(sketch, "E395", {"start": v(33.82, 453.76) * mm, "end": v(34.2, 453) * mm});
            skLineSegment(sketch, "E396", {"start": v(34.2, 453) * mm, "end": v(34.56, 452.24) * mm});
            skLineSegment(sketch, "E397", {"start": v(34.56, 452.24) * mm, "end": v(34.9, 451.48) * mm});
            skLineSegment(sketch, "E398", {"start": v(34.9, 451.48) * mm, "end": v(35.24, 450.7) * mm});
            skLineSegment(sketch, "E399", {"start": v(35.24, 450.7) * mm, "end": v(35.56, 449.94) * mm});
            skLineSegment(sketch, "E400", {"start": v(35.56, 449.94) * mm, "end": v(44.72, 427.63) * mm});
            skLineSegment(sketch, "E401", {"start": v(44.72, 427.63) * mm, "end": v(53.87, 405.32) * mm});
            skLineSegment(sketch, "E402", {"start": v(53.87, 405.32) * mm, "end": v(63.03, 383) * mm});
            skLineSegment(sketch, "E403", {"start": v(63.03, 383) * mm, "end": v(72.18, 360.69) * mm});
            skLineSegment(sketch, "E404", {"start": v(72.18, 360.69) * mm, "end": v(81.33, 338.37) * mm});
            skLineSegment(sketch, "E405", {"start": v(81.33, 338.37) * mm, "end": v(90.48, 316.06) * mm});
            skLineSegment(sketch, "E406", {"start": v(90.48, 316.06) * mm, "end": v(99.63, 293.74) * mm});
            skLineSegment(sketch, "E407", {"start": v(99.63, 293.74) * mm, "end": v(108.78, 271.43) * mm});
            skLineSegment(sketch, "E408", {"start": v(108.78, 271.43) * mm, "end": v(117.92, 249.1) * mm});
            skLineSegment(sketch, "E409", {"start": v(117.92, 249.1) * mm, "end": v(127.07, 226.79) * mm});
            skLineSegment(sketch, "E410", {"start": v(127.07, 226.79) * mm, "end": v(136.21, 204.47) * mm});
            skLineSegment(sketch, "E411", {"start": v(136.21, 204.47) * mm, "end": v(145.36, 182.15) * mm});
            skLineSegment(sketch, "E412", {"start": v(145.36, 182.15) * mm, "end": v(154.5, 159.83) * mm});
            skLineSegment(sketch, "E413", {"start": v(154.5, 159.83) * mm, "end": v(163.64, 137.52) * mm});
            skLineSegment(sketch, "E414", {"start": v(163.64, 137.52) * mm, "end": v(172.79, 115.2) * mm});
            skLineSegment(sketch, "E415", {"start": v(172.79, 115.2) * mm, "end": v(181.93, 92.88) * mm});
            skLineSegment(sketch, "E416", {"start": v(181.93, 92.88) * mm, "end": v(185.72, 83.61) * mm});
            skLineSegment(sketch, "E417", {"start": v(185.72, 83.61) * mm, "end": v(189.5, 74.34) * mm});
            skLineSegment(sketch, "E418", {"start": v(189.5, 74.34) * mm, "end": v(193.29, 65.07) * mm});
            skLineSegment(sketch, "E419", {"start": v(193.29, 65.07) * mm, "end": v(197.06, 55.8) * mm});
            skLineSegment(sketch, "E420", {"start": v(197.06, 55.8) * mm, "end": v(200.84, 46.52) * mm});
            skLineSegment(sketch, "E421", {"start": v(200.84, 46.52) * mm, "end": v(204.62, 37.24) * mm});
            skLineSegment(sketch, "E422", {"start": v(204.62, 37.24) * mm, "end": v(208.4, 27.97) * mm});
            skLineSegment(sketch, "E423", {"start": v(208.4, 27.97) * mm, "end": v(212.18, 18.7) * mm});
            skLineSegment(sketch, "E424", {"start": v(212.18, 18.7) * mm, "end": v(215.97, 9.43) * mm});
            skLineSegment(sketch, "E425", {"start": v(215.97, 9.43) * mm, "end": v(219.77, 0.17) * mm});
            skLineSegment(sketch, "E426", {"start": v(219.77, 0.17) * mm, "end": v(223.58, -9.1) * mm});
            skLineSegment(sketch, "E427", {"start": v(223.58, -9.1) * mm, "end": v(227.4, -18.35) * mm});
            skLineSegment(sketch, "E428", {"start": v(227.4, -18.35) * mm, "end": v(231.23, -27.6) * mm});
            skLineSegment(sketch, "E429", {"start": v(231.23, -27.6) * mm, "end": v(235.08, -36.85) * mm});
            skLineSegment(sketch, "E430", {"start": v(235.08, -36.85) * mm, "end": v(238.94, -46.09) * mm});
            skLineSegment(sketch, "E431", {"start": v(238.94, -46.09) * mm, "end": v(242.82, -55.32) * mm});
            skLineSegment(sketch, "E432", {"start": v(242.82, -55.32) * mm, "end": v(243.94, -58.51) * mm});
            skLineSegment(sketch, "E433", {"start": v(243.94, -58.51) * mm, "end": v(244.57, -61.61) * mm});
            skLineSegment(sketch, "E434", {"start": v(244.57, -61.61) * mm, "end": v(244.75, -64.6) * mm});
            skLineSegment(sketch, "E435", {"start": v(244.75, -64.6) * mm, "end": v(244.52, -67.46) * mm});
            skLineSegment(sketch, "E436", {"start": v(244.52, -67.46) * mm, "end": v(243.91, -70.18) * mm});
            skLineSegment(sketch, "E437", {"start": v(243.91, -70.18) * mm, "end": v(242.96, -72.74) * mm});
            skLineSegment(sketch, "E438", {"start": v(242.96, -72.74) * mm, "end": v(241.71, -75.12) * mm});
            skLineSegment(sketch, "E439", {"start": v(241.71, -75.12) * mm, "end": v(240.19, -77.32) * mm});
            skLineSegment(sketch, "E440", {"start": v(240.19, -77.32) * mm, "end": v(238.43, -79.3) * mm});
            skLineSegment(sketch, "E441", {"start": v(238.43, -79.3) * mm, "end": v(236.47, -81.07) * mm});
            skLineSegment(sketch, "E442", {"start": v(236.47, -81.07) * mm, "end": v(234.36, -82.6) * mm});
            skLineSegment(sketch, "E443", {"start": v(234.36, -82.6) * mm, "end": v(232.1, -83.88) * mm});
            skLineSegment(sketch, "E444", {"start": v(232.1, -83.88) * mm, "end": v(229.77, -84.89) * mm});
            skLineSegment(sketch, "E445", {"start": v(229.77, -84.89) * mm, "end": v(227.37, -85.61) * mm});
            skLineSegment(sketch, "E446", {"start": v(227.37, -85.61) * mm, "end": v(224.96, -86.04) * mm});
            skLineSegment(sketch, "E447", {"start": v(224.96, -86.04) * mm, "end": v(222.56, -86.15) * mm});
            skLineSegment(sketch, "E448", {"start": v(222.56, -86.15) * mm, "end": v(222.4, -86.14) * mm});
            skLineSegment(sketch, "E449", {"start": v(222.4, -86.14) * mm, "end": v(222.24, -86.14) * mm});
            skLineSegment(sketch, "E450", {"start": v(222.24, -86.14) * mm, "end": v(222.09, -86.14) * mm});
            skLineSegment(sketch, "E451", {"start": v(222.09, -86.14) * mm, "end": v(221.93, -86.14) * mm});
            skLineSegment(sketch, "E452", {"start": v(221.93, -86.14) * mm, "end": v(221.77, -86.14) * mm});
            skLineSegment(sketch, "E453", {"start": v(221.77, -86.14) * mm, "end": v(221.62, -86.14) * mm});
            skLineSegment(sketch, "E454", {"start": v(221.62, -86.14) * mm, "end": v(221.46, -86.14) * mm});
            skLineSegment(sketch, "E455", {"start": v(221.46, -86.14) * mm, "end": v(221.3, -86.14) * mm});
            skLineSegment(sketch, "E456", {"start": v(221.3, -86.14) * mm, "end": v(221.15, -86.14) * mm});
            skLineSegment(sketch, "E457", {"start": v(221.15, -86.14) * mm, "end": v(221, -86.14) * mm});
            skLineSegment(sketch, "E458", {"start": v(221, -86.14) * mm, "end": v(220.84, -86.14) * mm});
            skLineSegment(sketch, "E459", {"start": v(220.84, -86.14) * mm, "end": v(220.68, -86.15) * mm});
            skLineSegment(sketch, "E460", {"start": v(220.68, -86.15) * mm, "end": v(220.52, -86.15) * mm});
            skLineSegment(sketch, "E461", {"start": v(220.52, -86.15) * mm, "end": v(220.37, -86.15) * mm});
            skLineSegment(sketch, "E462", {"start": v(220.37, -86.15) * mm, "end": v(220.21, -86.15) * mm});
            skLineSegment(sketch, "E463", {"start": v(220.21, -86.15) * mm, "end": v(220.06, -86.15) * mm});
            skLineSegment(sketch, "E464", {"start": v(220.06, -86.15) * mm, "end": v(193.53, -86.15) * mm});
            skLineSegment(sketch, "E465", {"start": v(193.53, -86.15) * mm, "end": v(167, -86.15) * mm});
            skLineSegment(sketch, "E466", {"start": v(167, -86.15) * mm, "end": v(140.47, -86.15) * mm});
            skLineSegment(sketch, "E467", {"start": v(140.47, -86.15) * mm, "end": v(113.95, -86.15) * mm});
            skLineSegment(sketch, "E468", {"start": v(113.95, -86.15) * mm, "end": v(87.42, -86.15) * mm});
            skLineSegment(sketch, "E469", {"start": v(87.42, -86.15) * mm, "end": v(60.9, -86.15) * mm});
            skLineSegment(sketch, "E470", {"start": v(60.9, -86.15) * mm, "end": v(34.36, -86.15) * mm});
            skLineSegment(sketch, "E471", {"start": v(34.36, -86.15) * mm, "end": v(7.84, -86.14) * mm});
            skLineSegment(sketch, "E472", {"start": v(7.84, -86.14) * mm, "end": v(-18.7, -86.14) * mm});
            skLineSegment(sketch, "E473", {"start": v(-18.7, -86.14) * mm, "end": v(-45.22, -86.13) * mm});
            skLineSegment(sketch, "E474", {"start": v(-45.22, -86.13) * mm, "end": v(-71.75, -86.12) * mm});
            skLineSegment(sketch, "E475", {"start": v(-71.75, -86.12) * mm, "end": v(-98.27, -86.1) * mm});
            skLineSegment(sketch, "E476", {"start": v(-98.27, -86.1) * mm, "end": v(-124.8, -86.1) * mm});
            skLineSegment(sketch, "E477", {"start": v(-124.8, -86.1) * mm, "end": v(-151.33, -86.08) * mm});
            skLineSegment(sketch, "E478", {"start": v(-151.33, -86.08) * mm, "end": v(-177.86, -86.06) * mm});
            skLineSegment(sketch, "E479", {"start": v(-177.86, -86.06) * mm, "end": v(-204.38, -86.03) * mm});
            skLineSegment(sketch, "E480", {"start": v(-204.38, -86.03) * mm, "end": v(-205.23, -86.02) * mm});
            skLineSegment(sketch, "E481", {"start": v(-205.23, -86.02) * mm, "end": v(-206.09, -85.99) * mm});
            skLineSegment(sketch, "E482", {"start": v(-206.09, -85.99) * mm, "end": v(-206.95, -85.93) * mm});
            skLineSegment(sketch, "E483", {"start": v(-206.95, -85.93) * mm, "end": v(-207.82, -85.86) * mm});
            skLineSegment(sketch, "E484", {"start": v(-207.82, -85.86) * mm, "end": v(-208.69, -85.76) * mm});
            skLineSegment(sketch, "E485", {"start": v(-208.69, -85.76) * mm, "end": v(-209.55, -85.64) * mm});
            skLineSegment(sketch, "E486", {"start": v(-209.55, -85.64) * mm, "end": v(-210.42, -85.5) * mm});
            skLineSegment(sketch, "E487", {"start": v(-210.42, -85.5) * mm, "end": v(-211.28, -85.33) * mm});
            skLineSegment(sketch, "E488", {"start": v(-211.28, -85.33) * mm, "end": v(-212.14, -85.14) * mm});
            skLineSegment(sketch, "E489", {"start": v(-212.14, -85.14) * mm, "end": v(-212.99, -84.93) * mm});
            skLineSegment(sketch, "E490", {"start": v(-212.99, -84.93) * mm, "end": v(-213.82, -84.7) * mm});
            skLineSegment(sketch, "E491", {"start": v(-213.82, -84.7) * mm, "end": v(-214.65, -84.43) * mm});
            skLineSegment(sketch, "E492", {"start": v(-214.65, -84.43) * mm, "end": v(-215.46, -84.15) * mm});
            skLineSegment(sketch, "E493", {"start": v(-215.46, -84.15) * mm, "end": v(-216.26, -83.84) * mm});
            skLineSegment(sketch, "E494", {"start": v(-216.26, -83.84) * mm, "end": v(-217.04, -83.51) * mm});
            skLineSegment(sketch, "E495", {"start": v(-217.04, -83.51) * mm, "end": v(-217.8, -83.16) * mm});
            skLineSegment(sketch, "E496", {"start": v(-217.8, -83.16) * mm, "end": v(-219.21, -82.37) * mm});
            skLineSegment(sketch, "E497", {"start": v(-219.21, -82.37) * mm, "end": v(-220.53, -81.43) * mm});
            skLineSegment(sketch, "E498", {"start": v(-220.53, -81.43) * mm, "end": v(-221.74, -80.36) * mm});
            skLineSegment(sketch, "E499", {"start": v(-221.74, -80.36) * mm, "end": v(-222.85, -79.16) * mm});
            skLineSegment(sketch, "E500", {"start": v(-222.85, -79.16) * mm, "end": v(-223.86, -77.84) * mm});
            skLineSegment(sketch, "E501", {"start": v(-223.86, -77.84) * mm, "end": v(-224.76, -76.43) * mm});
            skLineSegment(sketch, "E502", {"start": v(-224.76, -76.43) * mm, "end": v(-225.56, -74.93) * mm});
            skLineSegment(sketch, "E503", {"start": v(-225.56, -74.93) * mm, "end": v(-226.24, -73.35) * mm});
            skLineSegment(sketch, "E504", {"start": v(-226.24, -73.35) * mm, "end": v(-226.8, -71.7) * mm});
            skLineSegment(sketch, "E505", {"start": v(-226.8, -71.7) * mm, "end": v(-227.25, -70) * mm});
            skLineSegment(sketch, "E506", {"start": v(-227.25, -70) * mm, "end": v(-227.58, -68.25) * mm});
            skLineSegment(sketch, "E507", {"start": v(-227.58, -68.25) * mm, "end": v(-227.78, -66.48) * mm});
            skLineSegment(sketch, "E508", {"start": v(-227.78, -66.48) * mm, "end": v(-227.86, -64.69) * mm});
            skLineSegment(sketch, "E509", {"start": v(-227.86, -64.69) * mm, "end": v(-227.8, -62.88) * mm});
            skLineSegment(sketch, "E510", {"start": v(-227.8, -62.88) * mm, "end": v(-227.63, -61.09) * mm});
            skLineSegment(sketch, "E511", {"start": v(-227.63, -61.09) * mm, "end": v(-227.31, -59.3) * mm});
            skLineSegment(sketch, "E512", {"start": v(-227.31, -59.3) * mm, "end": v(-226.86, -57.5) * mm});
            skLineSegment(sketch, "E513", {"start": v(-226.86, -57.5) * mm, "end": v(-226.3, -55.8) * mm});
            skLineSegment(sketch, "E514", {"start": v(-226.3, -55.8) * mm, "end": v(-225.63, -54.18) * mm});
            skLineSegment(sketch, "E515", {"start": v(-225.63, -54.18) * mm, "end": v(-224.87, -52.65) * mm});
            skLineSegment(sketch, "E516", {"start": v(-224.87, -52.65) * mm, "end": v(-224, -51.23) * mm});
            skLineSegment(sketch, "E517", {"start": v(-224, -51.23) * mm, "end": v(-223.05, -49.9) * mm});
            skLineSegment(sketch, "E518", {"start": v(-223.05, -49.9) * mm, "end": v(-222, -48.67) * mm});
            skLineSegment(sketch, "E519", {"start": v(-222, -48.67) * mm, "end": v(-220.86, -47.54) * mm});
            skLineSegment(sketch, "E520", {"start": v(-220.86, -47.54) * mm, "end": v(-219.62, -46.52) * mm});
            skLineSegment(sketch, "E521", {"start": v(-219.62, -46.52) * mm, "end": v(-218.3, -45.61) * mm});
            skLineSegment(sketch, "E522", {"start": v(-218.3, -45.61) * mm, "end": v(-216.9, -44.81) * mm});
            skLineSegment(sketch, "E523", {"start": v(-216.9, -44.81) * mm, "end": v(-215.43, -44.13) * mm});
            skLineSegment(sketch, "E524", {"start": v(-215.43, -44.13) * mm, "end": v(-213.87, -43.56) * mm});
            skLineSegment(sketch, "E525", {"start": v(-213.87, -43.56) * mm, "end": v(-212.24, -43.1) * mm});
            skLineSegment(sketch, "E526", {"start": v(-212.24, -43.1) * mm, "end": v(-210.53, -42.78) * mm});
            skLineSegment(sketch, "E527", {"start": v(-210.53, -42.78) * mm, "end": v(-208.76, -42.57) * mm});
            skLineSegment(sketch, "E528", {"start": v(-208.76, -42.57) * mm, "end": v(-208.35, -42.54) * mm});
            skLineSegment(sketch, "E529", {"start": v(-208.35, -42.54) * mm, "end": v(-207.95, -42.52) * mm});
            skLineSegment(sketch, "E530", {"start": v(-207.95, -42.52) * mm, "end": v(-207.54, -42.5) * mm});
            skLineSegment(sketch, "E531", {"start": v(-207.54, -42.5) * mm, "end": v(-207.14, -42.49) * mm});
            skLineSegment(sketch, "E532", {"start": v(-207.14, -42.49) * mm, "end": v(-206.73, -42.48) * mm});
            skLineSegment(sketch, "E533", {"start": v(-206.73, -42.48) * mm, "end": v(-206.32, -42.47) * mm});
            skLineSegment(sketch, "E534", {"start": v(-206.32, -42.47) * mm, "end": v(-205.92, -42.47) * mm});
            skLineSegment(sketch, "E535", {"start": v(-205.92, -42.47) * mm, "end": v(-205.51, -42.47) * mm});
            skLineSegment(sketch, "E536", {"start": v(-205.51, -42.47) * mm, "end": v(-205.1, -42.47) * mm});
            skLineSegment(sketch, "E537", {"start": v(-205.1, -42.47) * mm, "end": v(-204.7, -42.47) * mm});
            skLineSegment(sketch, "E538", {"start": v(-204.7, -42.47) * mm, "end": v(-204.3, -42.48) * mm});
            skLineSegment(sketch, "E539", {"start": v(-204.3, -42.48) * mm, "end": v(-203.89, -42.48) * mm});
            skLineSegment(sketch, "E540", {"start": v(-203.89, -42.48) * mm, "end": v(-203.48, -42.48) * mm});
            skLineSegment(sketch, "E541", {"start": v(-203.48, -42.48) * mm, "end": v(-203.07, -42.49) * mm});
            skLineSegment(sketch, "E542", {"start": v(-203.07, -42.49) * mm, "end": v(-202.67, -42.49) * mm});
            skLineSegment(sketch, "E543", {"start": v(-202.67, -42.49) * mm, "end": v(-202.26, -42.49) * mm});
            skLineSegment(sketch, "E544", {"start": v(-202.26, -42.49) * mm, "end": v(-178.14, -42.49) * mm});
            skLineSegment(sketch, "E545", {"start": v(-178.14, -42.49) * mm, "end": v(-154.02, -42.49) * mm});
            skLineSegment(sketch, "E546", {"start": v(-154.02, -42.49) * mm, "end": v(-129.9, -42.48) * mm});
            skLineSegment(sketch, "E547", {"start": v(-129.9, -42.48) * mm, "end": v(-105.77, -42.48) * mm});
            skLineSegment(sketch, "E548", {"start": v(-105.77, -42.48) * mm, "end": v(-81.65, -42.48) * mm});
            skLineSegment(sketch, "E549", {"start": v(-81.65, -42.48) * mm, "end": v(-57.53, -42.48) * mm});
            skLineSegment(sketch, "E550", {"start": v(-57.53, -42.48) * mm, "end": v(-33.4, -42.48) * mm});
            skLineSegment(sketch, "E551", {"start": v(-33.4, -42.48) * mm, "end": v(-9.29, -42.47) * mm});
            skLineSegment(sketch, "E552", {"start": v(-9.29, -42.47) * mm, "end": v(14.83, -42.47) * mm});
            skLineSegment(sketch, "E553", {"start": v(14.83, -42.47) * mm, "end": v(38.96, -42.47) * mm});
            skLineSegment(sketch, "E554", {"start": v(38.96, -42.47) * mm, "end": v(63.08, -42.47) * mm});
            skLineSegment(sketch, "E555", {"start": v(63.08, -42.47) * mm, "end": v(87.2, -42.47) * mm});
            skLineSegment(sketch, "E556", {"start": v(87.2, -42.47) * mm, "end": v(111.32, -42.47) * mm});
            skLineSegment(sketch, "E557", {"start": v(111.32, -42.47) * mm, "end": v(135.44, -42.46) * mm});
            skLineSegment(sketch, "E558", {"start": v(135.44, -42.46) * mm, "end": v(159.56, -42.46) * mm});
            skLineSegment(sketch, "E559", {"start": v(159.56, -42.46) * mm, "end": v(183.69, -42.46) * mm});
            skLineSegment(sketch, "E560", {"start": v(183.69, -42.46) * mm, "end": v(184.06, -42.46) * mm});
            skLineSegment(sketch, "E561", {"start": v(184.06, -42.46) * mm, "end": v(184.43, -42.46) * mm});
            skLineSegment(sketch, "E562", {"start": v(184.43, -42.46) * mm, "end": v(184.8, -42.46) * mm});
            skLineSegment(sketch, "E563", {"start": v(184.8, -42.46) * mm, "end": v(185.17, -42.46) * mm});
            skLineSegment(sketch, "E564", {"start": v(185.17, -42.46) * mm, "end": v(185.55, -42.46) * mm});
            skLineSegment(sketch, "E565", {"start": v(185.55, -42.46) * mm, "end": v(185.94, -42.46) * mm});
            skLineSegment(sketch, "E566", {"start": v(185.94, -42.46) * mm, "end": v(186.32, -42.46) * mm});
            skLineSegment(sketch, "E567", {"start": v(186.32, -42.46) * mm, "end": v(186.72, -42.46) * mm});
            skLineSegment(sketch, "E568", {"start": v(186.72, -42.46) * mm, "end": v(187.12, -42.46) * mm});
            skLineSegment(sketch, "E569", {"start": v(187.12, -42.46) * mm, "end": v(187.53, -42.46) * mm});
            skLineSegment(sketch, "E570", {"start": v(187.53, -42.46) * mm, "end": v(187.95, -42.46) * mm});
            skLineSegment(sketch, "E571", {"start": v(187.95, -42.46) * mm, "end": v(188.38, -42.46) * mm});
            skLineSegment(sketch, "E572", {"start": v(188.38, -42.46) * mm, "end": v(188.82, -42.46) * mm});
            skLineSegment(sketch, "E573", {"start": v(188.82, -42.46) * mm, "end": v(189.28, -42.46) * mm});
            skLineSegment(sketch, "E574", {"start": v(189.28, -42.46) * mm, "end": v(189.74, -42.46) * mm});
            skLineSegment(sketch, "E575", {"start": v(189.74, -42.46) * mm, "end": v(190.22, -42.46) * mm});
            skSolve(sketch);
        }
        {
            var Q0;
            Q0=qCreatedBy(makeId("Top.planeOp"),FACE);
            var sketch = newSketch(context, id + "F1", { "sketchPlane" : qUnion([Q0])});
            skCircle(sketch, "E576", {"center": v(0, 448) * mm, "radius": 25 * mm});
            skCircle(sketch, "E577", {"center": v(220, -65) * mm, "radius": 25 * mm});
            skCircle(sketch, "E578", {"center": v(-220, -65) * mm, "radius": 25 * mm});
            skCircle(sketch, "E579", {"center": v(-300, -262) * mm, "radius": 25 * mm});
            skCircle(sketch, "E580", {"center": v(300, -262) * mm, "radius": 25 * mm});
            skCircle(sketch, "E581", {"center": v(380, -447) * mm, "radius": 25 * mm});
            skCircle(sketch, "E582", {"center": v(-380, -447) * mm, "radius": 25 * mm});
            skLineSegment(sketch, "E583", {"start": v(22.98, 457.85) * mm, "end": v(242.98, -55.15) * mm});
            skLineSegment(sketch, "E584", {"start": v(-22.98, 438.15) * mm, "end": v(197.02, -74.85) * mm});
            skLineSegment(sketch, "E585", {"start": v(220, -90) * mm, "end": v(-220, -90) * mm});
            skLineSegment(sketch, "E586", {"start": v(220, -40) * mm, "end": v(-220, -40) * mm});
            skLineSegment(sketch, "E587", {"start": v(-300, -237) * mm, "end": v(300, -237) * mm});
            skLineSegment(sketch, "E588", {"start": v(-300, -287) * mm, "end": v(300, -287) * mm});
            skLineSegment(sketch, "E589", {"start": v(-322.95, -252.08) * mm, "end": v(-402.95, -437.08) * mm});
            skLineSegment(sketch, "E590", {"start": v(-357.05, -456.92) * mm, "end": v(-277.05, -271.92) * mm});
            skLineSegment(sketch, "E591", {"start": v(322.95, -252.08) * mm, "end": v(402.95, -437.08) * mm});
            skLineSegment(sketch, "E592", {"start": v(277.05, -271.92) * mm, "end": v(357.05, -456.92) * mm});
            skSolve(sketch);
        }
        {
            var Q0;
            Q0=qSketchRegion(id+"F1",true);
            extrude(context, id + "F2", {"entities" : qUnion([Q0]), "depth" : 100 * mm, "offsetDistance" : 25 * mm});
        }
        {
            var Q0;
            Q0=makeQuery(id+"F2.opExtrude","CAP_FACE",FACE,{"disambiguationData":[OSD([sQuery(id+"F1.wireOp",EDGE,"E576"),sQuery(id+"F1.wireOp",EDGE,"E577"),sQuery(id+"F1.wireOp",EDGE,"E578"),sQuery(id+"F1.wireOp",EDGE,"E583"),sQuery(id+"F1.wireOp",EDGE,"E584"),sQuery(id+"F1.wireOp",EDGE,"E585"),sQuery(id+"F1.wireOp",EDGE,"E586")])],"isStart":false});
            var sketch = newSketch(context, id + "F3", { "sketchPlane" : qUnion([Q0])});
            skArc(sketch, "E593.0.0", {"start": v(22.98, 457.85) * mm, "mid": v(-9.85, 470.98) * mm, "end": v(-22.98, 438.15) * mm});
            skLineSegment(sketch, "E593.0.1", {"start": v(-22.98, 438.15) * mm, "end": v(182.08, -40) * mm});
            skLineSegment(sketch, "E593.0.2", {"start": v(182.08, -40) * mm, "end": v(-220, -40) * mm});
            skArc(sketch, "E593.0.3", {"start": v(-220, -40) * mm, "mid": v(-245, -65) * mm, "end": v(-220, -90) * mm});
            skLineSegment(sketch, "E593.0.4", {"start": v(-220, -90) * mm, "end": v(220, -90) * mm});
            skArc(sketch, "E593.0.5", {"start": v(220, -90) * mm, "mid": v(240.87, -78.76) * mm, "end": v(242.98, -55.15) * mm});
            skLineSegment(sketch, "E593.0.6", {"start": v(242.98, -55.15) * mm, "end": v(22.98, 457.85) * mm});
            skArc(sketch, "E594.0.0", {"start": v(357.05, -456.92) * mm, "mid": v(389.92, -469.95) * mm, "end": v(402.95, -437.08) * mm});
            skLineSegment(sketch, "E594.0.1", {"start": v(402.95, -437.08) * mm, "end": v(322.95, -252.08) * mm});
            skArc(sketch, "E594.0.2", {"start": v(322.95, -252.08) * mm, "mid": v(313.73, -241.1) * mm, "end": v(300, -237) * mm});
            skLineSegment(sketch, "E594.0.3", {"start": v(300, -237) * mm, "end": v(-300, -237) * mm});
            skArc(sketch, "E594.0.4", {"start": v(-300, -237) * mm, "mid": v(-313.73, -241.1) * mm, "end": v(-322.95, -252.08) * mm});
            skLineSegment(sketch, "E594.0.5", {"start": v(-322.95, -252.08) * mm, "end": v(-402.95, -437.08) * mm});
            skArc(sketch, "E594.0.6", {"start": v(-402.95, -437.08) * mm, "mid": v(-389.92, -469.95) * mm, "end": v(-357.05, -456.92) * mm});
            skLineSegment(sketch, "E594.0.7", {"start": v(-357.05, -456.92) * mm, "end": v(-283.57, -287) * mm});
            skLineSegment(sketch, "E594.0.8", {"start": v(-283.57, -287) * mm, "end": v(283.57, -287) * mm});
            skLineSegment(sketch, "E594.0.9", {"start": v(283.57, -287) * mm, "end": v(357.05, -456.92) * mm});
            skLineSegment(sketch, "E595", {"start": v(-320.31, -371.96) * mm, "end": v(-322.95, -252.08) * mm});
            skLineSegment(sketch, "E596", {"start": v(32.58, 308.6) * mm, "end": v(91.76, 297.46) * mm});
            skSolve(sketch);
        }
        {
            var Q0;
            {var subQ0=sQuery(id+"F3.wireOp",EDGE,"E593.0.0");Q0=makeQuery(id+"F3.imprint","IMPRINT",FACE,{"disambiguationData":[TD([[makeQuery(id+"F3.imprint","IMPRINT",EDGE,{"derivedFrom":subQ0}),1.0]])]});}
            var Q1;
            Q1=makeQuery(id+"F3.imprint","IMPRINT",FACE,{"disambiguationData":[TD([[makeQuery(id+"F3.imprint","IMPRINT",EDGE,{"derivedFrom":sQuery(id+"F3.wireOp",EDGE,"E594.0.5")}),1.0]])]});
            extrude(context, id + "F4", {"entities" : qUnion([Q0, Q1]), "depth" : 400 * mm, "offsetDistance" : 25 * mm, "hasSecondDirection" : true, "secondDirectionOppositeDirection" : false, "secondDirectionDepth" : 312 * mm});
        }
        {
            var Q0;
            Q0=makeQuery(id+"F2.opExtrude","CAP_FACE",FACE,{"disambiguationData":[OSD([sQuery(id+"F1.wireOp",EDGE,"E576"),sQuery(id+"F1.wireOp",EDGE,"E577"),sQuery(id+"F1.wireOp",EDGE,"E578"),sQuery(id+"F1.wireOp",EDGE,"E583"),sQuery(id+"F1.wireOp",EDGE,"E584"),sQuery(id+"F1.wireOp",EDGE,"E585"),sQuery(id+"F1.wireOp",EDGE,"E586")])],"isStart":false});
            var sketch = newSketch(context, id + "F5", { "sketchPlane" : qUnion([Q0])});
            skArc(sketch, "E597.0.0", {"start": v(22.98, 457.85) * mm, "mid": v(-9.85, 470.98) * mm, "end": v(-22.98, 438.15) * mm});
            skLineSegment(sketch, "E597.0.1", {"start": v(-22.98, 438.15) * mm, "end": v(182.08, -40) * mm});
            skLineSegment(sketch, "E597.0.2", {"start": v(182.08, -40) * mm, "end": v(-220, -40) * mm});
            skArc(sketch, "E597.0.3", {"start": v(-220, -40) * mm, "mid": v(-245, -65) * mm, "end": v(-220, -90) * mm});
            skLineSegment(sketch, "E597.0.4", {"start": v(-220, -90) * mm, "end": v(220, -90) * mm});
            skArc(sketch, "E597.0.5", {"start": v(220, -90) * mm, "mid": v(240.87, -78.76) * mm, "end": v(242.98, -55.15) * mm});
            skLineSegment(sketch, "E597.0.6", {"start": v(242.98, -55.15) * mm, "end": v(22.98, 457.85) * mm});
            skLineSegment(sketch, "E598", {"start": v(20.3, 337.23) * mm, "end": v(54.68, 383.93) * mm});
            skLineSegment(sketch, "E599", {"start": v(150.98, 32.5) * mm, "end": v(196.94, 52.2) * mm});
            skArc(sketch, "E600.0.0", {"start": v(357.05, -456.92) * mm, "mid": v(389.92, -469.95) * mm, "end": v(402.95, -437.08) * mm});
            skLineSegment(sketch, "E600.0.1", {"start": v(402.95, -437.08) * mm, "end": v(322.95, -252.08) * mm});
            skArc(sketch, "E600.0.2", {"start": v(322.95, -252.08) * mm, "mid": v(313.73, -241.1) * mm, "end": v(300, -237) * mm});
            skLineSegment(sketch, "E600.0.3", {"start": v(300, -237) * mm, "end": v(-300, -237) * mm});
            skArc(sketch, "E600.0.4", {"start": v(-300, -237) * mm, "mid": v(-313.73, -241.1) * mm, "end": v(-322.95, -252.08) * mm});
            skLineSegment(sketch, "E600.0.5", {"start": v(-322.95, -252.08) * mm, "end": v(-402.95, -437.08) * mm});
            skArc(sketch, "E600.0.6", {"start": v(-402.95, -437.08) * mm, "mid": v(-389.92, -469.95) * mm, "end": v(-357.05, -456.92) * mm});
            skLineSegment(sketch, "E600.0.7", {"start": v(-357.05, -456.92) * mm, "end": v(-283.57, -287) * mm});
            skLineSegment(sketch, "E600.0.8", {"start": v(-283.57, -287) * mm, "end": v(283.57, -287) * mm});
            skLineSegment(sketch, "E600.0.9", {"start": v(283.57, -287) * mm, "end": v(357.05, -456.92) * mm});
            skLineSegment(sketch, "E601", {"start": v(215.1, -237) * mm, "end": v(215.1, -287) * mm});
            skSolve(sketch);
        }
        {
            var Q0;
            Q0=makeQuery(id+"F5.imprint","IMPRINT",FACE,{"disambiguationData":[TD([[makeQuery(id+"F5.imprint","IMPRINT",EDGE,{"derivedFrom":sQuery(id+"F5.wireOp",EDGE,"E600.0.0")}),1.0]])]});
            var Q1;
            {var subQ0=sQuery(id+"F5.wireOp",EDGE,"E598");Q1=makeQuery(id+"F5.imprint","IMPRINT",FACE,{"disambiguationData":[TD([[makeQuery(id+"F5.imprint","IMPRINT",EDGE,{"derivedFrom":subQ0}),-1.0]])]});}
            extrude(context, id + "F6", {"entities" : qUnion([Q0, Q1]), "depth" : 184 * mm, "offsetDistance" : 25 * mm, "hasSecondDirection" : true, "secondDirectionOppositeDirection" : false, "secondDirectionDepth" : 75 * mm});
        }
        {
            var Q0;
            Q0=makeQuery(id+"F2.opExtrude","CAP_FACE",FACE,{"disambiguationData":[OSD([sQuery(id+"F1.wireOp",EDGE,"E576"),sQuery(id+"F1.wireOp",EDGE,"E577"),sQuery(id+"F1.wireOp",EDGE,"E578"),sQuery(id+"F1.wireOp",EDGE,"E583"),sQuery(id+"F1.wireOp",EDGE,"E584"),sQuery(id+"F1.wireOp",EDGE,"E585"),sQuery(id+"F1.wireOp",EDGE,"E586")])],"isStart":false});
            var sketch = newSketch(context, id + "F7", { "sketchPlane" : qUnion([Q0])});
            skArc(sketch, "E602.0.0", {"start": v(22.98, 457.85) * mm, "mid": v(-9.85, 470.98) * mm, "end": v(-22.98, 438.15) * mm});
            skLineSegment(sketch, "E602.0.1", {"start": v(-22.98, 438.15) * mm, "end": v(182.08, -40) * mm});
            skLineSegment(sketch, "E602.0.2", {"start": v(182.08, -40) * mm, "end": v(-220, -40) * mm});
            skArc(sketch, "E602.0.3", {"start": v(-220, -40) * mm, "mid": v(-245, -65) * mm, "end": v(-220, -90) * mm});
            skLineSegment(sketch, "E602.0.4", {"start": v(-220, -90) * mm, "end": v(220, -90) * mm});
            skArc(sketch, "E602.0.5", {"start": v(220, -90) * mm, "mid": v(240.87, -78.76) * mm, "end": v(242.98, -55.15) * mm});
            skLineSegment(sketch, "E602.0.6", {"start": v(242.98, -55.15) * mm, "end": v(22.98, 457.85) * mm});
            skLineSegment(sketch, "E603", {"start": v(98.56, -40) * mm, "end": v(0, -90) * mm});
            skLineSegment(sketch, "E604", {"start": v(130.23, 80.9) * mm, "end": v(191.68, 64.47) * mm});
            skArc(sketch, "E605.0.0", {"start": v(357.05, -456.92) * mm, "mid": v(389.92, -469.95) * mm, "end": v(402.95, -437.08) * mm});
            skLineSegment(sketch, "E605.0.1", {"start": v(402.95, -437.08) * mm, "end": v(322.95, -252.08) * mm});
            skArc(sketch, "E605.0.2", {"start": v(322.95, -252.08) * mm, "mid": v(313.73, -241.1) * mm, "end": v(300, -237) * mm});
            skLineSegment(sketch, "E605.0.3", {"start": v(300, -237) * mm, "end": v(-300, -237) * mm});
            skArc(sketch, "E605.0.4", {"start": v(-300, -237) * mm, "mid": v(-313.73, -241.1) * mm, "end": v(-322.95, -252.08) * mm});
            skLineSegment(sketch, "E605.0.5", {"start": v(-322.95, -252.08) * mm, "end": v(-402.95, -437.08) * mm});
            skArc(sketch, "E605.0.6", {"start": v(-402.95, -437.08) * mm, "mid": v(-389.92, -469.95) * mm, "end": v(-357.05, -456.92) * mm});
            skLineSegment(sketch, "E605.0.7", {"start": v(-357.05, -456.92) * mm, "end": v(-283.57, -287) * mm});
            skLineSegment(sketch, "E605.0.8", {"start": v(-283.57, -287) * mm, "end": v(283.57, -287) * mm});
            skLineSegment(sketch, "E605.0.9", {"start": v(283.57, -287) * mm, "end": v(357.05, -456.92) * mm});
            skLineSegment(sketch, "E606", {"start": v(-329.4, -392.96) * mm, "end": v(-365.97, -351.57) * mm});
            skLineSegment(sketch, "E607", {"start": v(-49.97, -287) * mm, "end": v(50.41, -237) * mm});
            skSolve(sketch);
        }
        {
            var Q0;
            {var subQ1=sQuery(id+"F7.wireOp",EDGE,"E605.0.4");Q0=makeQuery(id+"F7.imprint","IMPRINT",FACE,{"disambiguationData":[TD([[makeQuery(id+"F7.imprint","IMPRINT",EDGE,{"derivedFrom":subQ1}),1.0]])]});}
            var Q1;
            {var subQ0=sQuery(id+"F7.wireOp",EDGE,"E602.0.5");Q1=makeQuery(id+"F7.imprint","IMPRINT",FACE,{"disambiguationData":[TD([[makeQuery(id+"F7.imprint","IMPRINT",EDGE,{"derivedFrom":subQ0}),1.0]])]});}
            extrude(context, id + "F8", {"entities" : qUnion([Q0, Q1]), "oppositeDirection" : true, "depth" : 241 * mm, "offsetDistance" : 25 * mm, "hasSecondDirection" : true, "secondDirectionOppositeDirection" : true, "secondDirectionDepth" : 112 * mm});
        }
        {
            var Q0;
            Q0=makeQuery(id+"F2.opExtrude","CAP_FACE",FACE,{"disambiguationData":[OSD([sQuery(id+"F1.wireOp",EDGE,"E576"),sQuery(id+"F1.wireOp",EDGE,"E577"),sQuery(id+"F1.wireOp",EDGE,"E578"),sQuery(id+"F1.wireOp",EDGE,"E583"),sQuery(id+"F1.wireOp",EDGE,"E584"),sQuery(id+"F1.wireOp",EDGE,"E585"),sQuery(id+"F1.wireOp",EDGE,"E586")])],"isStart":false});
            var sketch = newSketch(context, id + "F9", { "sketchPlane" : qUnion([Q0])});
            skArc(sketch, "E608.0.0", {"start": v(22.98, 457.85) * mm, "mid": v(-9.85, 470.98) * mm, "end": v(-22.98, 438.15) * mm});
            skLineSegment(sketch, "E608.0.1", {"start": v(-22.98, 438.15) * mm, "end": v(182.08, -40) * mm});
            skLineSegment(sketch, "E608.0.2", {"start": v(182.08, -40) * mm, "end": v(-220, -40) * mm});
            skArc(sketch, "E608.0.3", {"start": v(-220, -40) * mm, "mid": v(-245, -65) * mm, "end": v(-220, -90) * mm});
            skLineSegment(sketch, "E608.0.4", {"start": v(-220, -90) * mm, "end": v(220, -90) * mm});
            skArc(sketch, "E608.0.5", {"start": v(220, -90) * mm, "mid": v(240.87, -78.76) * mm, "end": v(242.98, -55.15) * mm});
            skLineSegment(sketch, "E608.0.6", {"start": v(242.98, -55.15) * mm, "end": v(22.98, 457.85) * mm});
            skArc(sketch, "E609.0.0", {"start": v(357.05, -456.92) * mm, "mid": v(389.92, -469.95) * mm, "end": v(402.95, -437.08) * mm});
            skLineSegment(sketch, "E609.0.1", {"start": v(402.95, -437.08) * mm, "end": v(322.95, -252.08) * mm});
            skArc(sketch, "E609.0.2", {"start": v(322.95, -252.08) * mm, "mid": v(313.73, -241.1) * mm, "end": v(300, -237) * mm});
            skLineSegment(sketch, "E609.0.3", {"start": v(300, -237) * mm, "end": v(-300, -237) * mm});
            skArc(sketch, "E609.0.4", {"start": v(-300, -237) * mm, "mid": v(-313.73, -241.1) * mm, "end": v(-322.95, -252.08) * mm});
            skLineSegment(sketch, "E609.0.5", {"start": v(-322.95, -252.08) * mm, "end": v(-402.95, -437.08) * mm});
            skArc(sketch, "E609.0.6", {"start": v(-402.95, -437.08) * mm, "mid": v(-389.92, -469.95) * mm, "end": v(-357.05, -456.92) * mm});
            skLineSegment(sketch, "E609.0.7", {"start": v(-357.05, -456.92) * mm, "end": v(-283.57, -287) * mm});
            skLineSegment(sketch, "E609.0.8", {"start": v(-283.57, -287) * mm, "end": v(283.57, -287) * mm});
            skLineSegment(sketch, "E609.0.9", {"start": v(283.57, -287) * mm, "end": v(357.05, -456.92) * mm});
            skLineSegment(sketch, "E610", {"start": v(-62.86, -287) * mm, "end": v(-154.23, -237) * mm});
            skLineSegment(sketch, "E611", {"start": v(322.95, -252.08) * mm, "end": v(283.57, -287) * mm});
            skLineSegment(sketch, "E612", {"start": v(182.08, -40) * mm, "end": v(182.08, -90) * mm});
            skSolve(sketch);
        }
        {
            var Q0;
            Q0=makeQuery(id+"F9.imprint","IMPRINT",FACE,{"disambiguationData":[TD([[makeQuery(id+"F9.imprint","IMPRINT",EDGE,{"derivedFrom":sQuery(id+"F9.wireOp",EDGE,"E608.0.2")}),1.0]])]});
            var Q1;
            {var subQ4=sQuery(id+"F9.wireOp",EDGE,"E609.0.2");Q1=makeQuery(id+"F9.imprint","IMPRINT",FACE,{"disambiguationData":[TD([[makeQuery(id+"F9.imprint","IMPRINT",EDGE,{"derivedFrom":subQ4}),1.0]])]});}
            extrude(context, id + "F10", {"entities" : qUnion([Q0, Q1]), "oppositeDirection" : true, "depth" : 534 * mm, "offsetDistance" : 25 * mm, "hasSecondDirection" : true, "secondDirectionOppositeDirection" : true, "secondDirectionDepth" : 361 * mm});
        }
        {
            var Q0;
            Q0=makeQuery(id+"F6.opExtrude","SWEPT_EDGE",EDGE,{"disambiguationData":[OSD([sQuery(id+"F5.wireOp",EDGE,"E597.0.6"),sQuery(id+"F5.wireOp",EDGE,"E598")])]});
            var Q1;
            Q1=makeQuery(id+"F8.opExtrude","SWEPT_EDGE",EDGE,{"disambiguationData":[OSD([sQuery(id+"F7.wireOp",EDGE,"E602.0.1"),sQuery(id+"F7.wireOp",EDGE,"E604")])]});
            var Q2;
            Q2=makeQuery(id+"F8.opExtrude","SWEPT_EDGE",EDGE,{"disambiguationData":[OSD([sQuery(id+"F7.wireOp",EDGE,"E605.0.3"),sQuery(id+"F7.wireOp",EDGE,"E607")])]});
            var Q3;
            Q3=makeQuery(id+"F8.opExtrude","SWEPT_EDGE",EDGE,{"disambiguationData":[OSD([sQuery(id+"F7.wireOp",EDGE,"E602.0.4"),sQuery(id+"F7.wireOp",EDGE,"E603")])]});
            var Q4;
            Q4=makeQuery(id+"F4.opExtrude","SWEPT_EDGE",EDGE,{"disambiguationData":[OSD([sQuery(id+"F3.wireOp",EDGE,"E594.0.4"),sQuery(id+"F3.wireOp",EDGE,"E594.0.5"),sQuery(id+"F3.wireOp",EDGE,"E595")])]});
            chamfer(context, id + "F11", {"entities" : qUnion([Q0, Q1, Q2, Q3, Q4]), "width" : 30 * mm, "tangentPropagation" : true});
        }
    });
